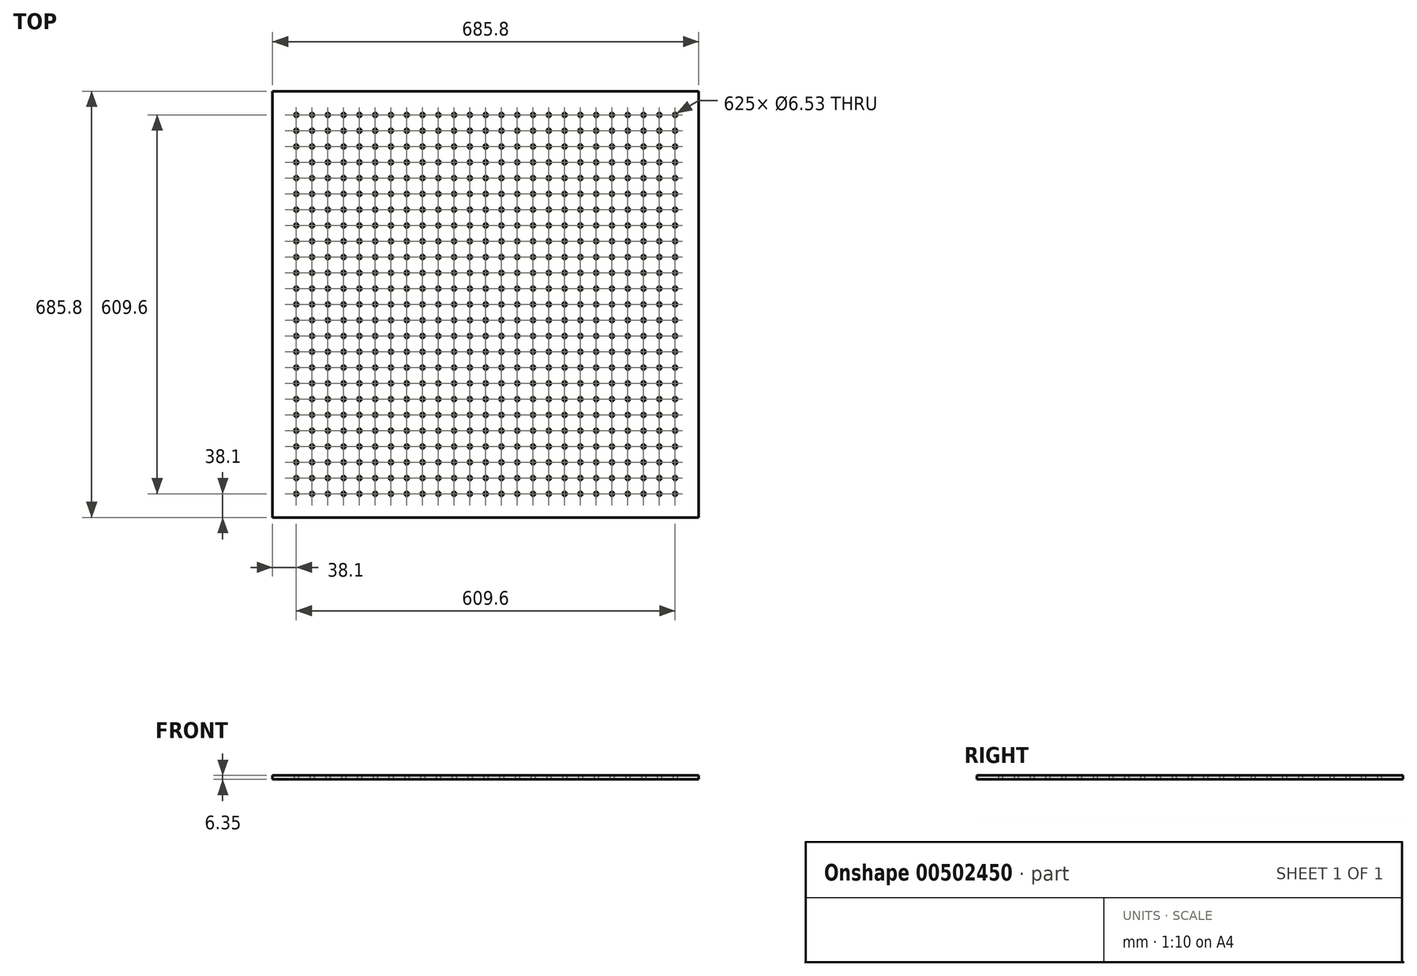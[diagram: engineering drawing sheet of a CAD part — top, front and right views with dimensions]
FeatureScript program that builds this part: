
annotation { "Feature Type Name" : "Feature", "Feature Type Description" : "" }
export const myFeature = defineFeature(function(context is Context, id is Id, definition is map)
    precondition{}
    {
        {
            var Q0;
            Q0=qCreatedBy(makeId("Top.planeOp"),FACE);
            var sketch = newSketch(context, id + "F0", { "sketchPlane" : qUnion([Q0])});
            skLineSegment(sketch, "E0.bottom", {"start": v(0, 685.8) * mm, "end": v(685.8, 685.8) * mm});
            skLineSegment(sketch, "E0.top", {"start": v(0, 0) * mm, "end": v(685.8, 0) * mm});
            skLineSegment(sketch, "E0.left", {"start": v(0, 685.8) * mm, "end": v(0, 0) * mm});
            skLineSegment(sketch, "E0.right", {"start": v(685.8, 685.8) * mm, "end": v(685.8, 0) * mm});
            skPoint(sketch, "E1", {"position": v(38.1, 38.1) * mm});
            skPoint(sketch, "E2.0.1.0", {"position": v(38.1, 63.5) * mm});
            skPoint(sketch, "E2.0.2.0", {"position": v(38.1, 88.9) * mm});
            skPoint(sketch, "E2.0.3.0", {"position": v(38.1, 114.3) * mm});
            skPoint(sketch, "E2.0.4.0", {"position": v(38.1, 139.7) * mm});
            skPoint(sketch, "E2.0.5.0", {"position": v(38.1, 165.1) * mm});
            skPoint(sketch, "E2.0.6.0", {"position": v(38.1, 190.5) * mm});
            skPoint(sketch, "E2.0.7.0", {"position": v(38.1, 215.9) * mm});
            skPoint(sketch, "E2.0.8.0", {"position": v(38.1, 241.3) * mm});
            skPoint(sketch, "E2.0.9.0", {"position": v(38.1, 266.7) * mm});
            skPoint(sketch, "E2.0.10.0", {"position": v(38.1, 292.1) * mm});
            skPoint(sketch, "E2.0.11.0", {"position": v(38.1, 317.5) * mm});
            skPoint(sketch, "E2.0.12.0", {"position": v(38.1, 342.9) * mm});
            skPoint(sketch, "E2.0.13.0", {"position": v(38.1, 368.3) * mm});
            skPoint(sketch, "E2.0.14.0", {"position": v(38.1, 393.7) * mm});
            skPoint(sketch, "E2.0.15.0", {"position": v(38.1, 419.1) * mm});
            skPoint(sketch, "E2.0.16.0", {"position": v(38.1, 444.5) * mm});
            skPoint(sketch, "E2.0.17.0", {"position": v(38.1, 469.9) * mm});
            skPoint(sketch, "E2.0.18.0", {"position": v(38.1, 495.3) * mm});
            skPoint(sketch, "E2.0.19.0", {"position": v(38.1, 520.7) * mm});
            skPoint(sketch, "E2.0.20.0", {"position": v(38.1, 546.1) * mm});
            skPoint(sketch, "E2.0.21.0", {"position": v(38.1, 571.5) * mm});
            skPoint(sketch, "E2.0.22.0", {"position": v(38.1, 596.9) * mm});
            skPoint(sketch, "E2.0.23.0", {"position": v(38.1, 622.3) * mm});
            skPoint(sketch, "E2.0.24.0", {"position": v(38.1, 647.7) * mm});
            skPoint(sketch, "E2.1.0.0", {"position": v(63.5, 38.1) * mm});
            skPoint(sketch, "E2.1.1.0", {"position": v(63.5, 63.5) * mm});
            skPoint(sketch, "E2.1.2.0", {"position": v(63.5, 88.9) * mm});
            skPoint(sketch, "E2.1.3.0", {"position": v(63.5, 114.3) * mm});
            skPoint(sketch, "E2.1.4.0", {"position": v(63.5, 139.7) * mm});
            skPoint(sketch, "E2.1.5.0", {"position": v(63.5, 165.1) * mm});
            skPoint(sketch, "E2.1.6.0", {"position": v(63.5, 190.5) * mm});
            skPoint(sketch, "E2.1.7.0", {"position": v(63.5, 215.9) * mm});
            skPoint(sketch, "E2.1.8.0", {"position": v(63.5, 241.3) * mm});
            skPoint(sketch, "E2.1.9.0", {"position": v(63.5, 266.7) * mm});
            skPoint(sketch, "E2.1.10.0", {"position": v(63.5, 292.1) * mm});
            skPoint(sketch, "E2.1.11.0", {"position": v(63.5, 317.5) * mm});
            skPoint(sketch, "E2.1.12.0", {"position": v(63.5, 342.9) * mm});
            skPoint(sketch, "E2.1.13.0", {"position": v(63.5, 368.3) * mm});
            skPoint(sketch, "E2.1.14.0", {"position": v(63.5, 393.7) * mm});
            skPoint(sketch, "E2.1.15.0", {"position": v(63.5, 419.1) * mm});
            skPoint(sketch, "E2.1.16.0", {"position": v(63.5, 444.5) * mm});
            skPoint(sketch, "E2.1.17.0", {"position": v(63.5, 469.9) * mm});
            skPoint(sketch, "E2.1.18.0", {"position": v(63.5, 495.3) * mm});
            skPoint(sketch, "E2.1.19.0", {"position": v(63.5, 520.7) * mm});
            skPoint(sketch, "E2.1.20.0", {"position": v(63.5, 546.1) * mm});
            skPoint(sketch, "E2.1.21.0", {"position": v(63.5, 571.5) * mm});
            skPoint(sketch, "E2.1.22.0", {"position": v(63.5, 596.9) * mm});
            skPoint(sketch, "E2.1.23.0", {"position": v(63.5, 622.3) * mm});
            skPoint(sketch, "E2.1.24.0", {"position": v(63.5, 647.7) * mm});
            skPoint(sketch, "E2.2.0.0", {"position": v(88.9, 38.1) * mm});
            skPoint(sketch, "E2.2.1.0", {"position": v(88.9, 63.5) * mm});
            skPoint(sketch, "E2.2.2.0", {"position": v(88.9, 88.9) * mm});
            skPoint(sketch, "E2.2.3.0", {"position": v(88.9, 114.3) * mm});
            skPoint(sketch, "E2.2.4.0", {"position": v(88.9, 139.7) * mm});
            skPoint(sketch, "E2.2.5.0", {"position": v(88.9, 165.1) * mm});
            skPoint(sketch, "E2.2.6.0", {"position": v(88.9, 190.5) * mm});
            skPoint(sketch, "E2.2.7.0", {"position": v(88.9, 215.9) * mm});
            skPoint(sketch, "E2.2.8.0", {"position": v(88.9, 241.3) * mm});
            skPoint(sketch, "E2.2.9.0", {"position": v(88.9, 266.7) * mm});
            skPoint(sketch, "E2.2.10.0", {"position": v(88.9, 292.1) * mm});
            skPoint(sketch, "E2.2.11.0", {"position": v(88.9, 317.5) * mm});
            skPoint(sketch, "E2.2.12.0", {"position": v(88.9, 342.9) * mm});
            skPoint(sketch, "E2.2.13.0", {"position": v(88.9, 368.3) * mm});
            skPoint(sketch, "E2.2.14.0", {"position": v(88.9, 393.7) * mm});
            skPoint(sketch, "E2.2.15.0", {"position": v(88.9, 419.1) * mm});
            skPoint(sketch, "E2.2.16.0", {"position": v(88.9, 444.5) * mm});
            skPoint(sketch, "E2.2.17.0", {"position": v(88.9, 469.9) * mm});
            skPoint(sketch, "E2.2.18.0", {"position": v(88.9, 495.3) * mm});
            skPoint(sketch, "E2.2.19.0", {"position": v(88.9, 520.7) * mm});
            skPoint(sketch, "E2.2.20.0", {"position": v(88.9, 546.1) * mm});
            skPoint(sketch, "E2.2.21.0", {"position": v(88.9, 571.5) * mm});
            skPoint(sketch, "E2.2.22.0", {"position": v(88.9, 596.9) * mm});
            skPoint(sketch, "E2.2.23.0", {"position": v(88.9, 622.3) * mm});
            skPoint(sketch, "E2.2.24.0", {"position": v(88.9, 647.7) * mm});
            skPoint(sketch, "E2.3.0.0", {"position": v(114.3, 38.1) * mm});
            skPoint(sketch, "E2.3.1.0", {"position": v(114.3, 63.5) * mm});
            skPoint(sketch, "E2.3.2.0", {"position": v(114.3, 88.9) * mm});
            skPoint(sketch, "E2.3.3.0", {"position": v(114.3, 114.3) * mm});
            skPoint(sketch, "E2.3.4.0", {"position": v(114.3, 139.7) * mm});
            skPoint(sketch, "E2.3.5.0", {"position": v(114.3, 165.1) * mm});
            skPoint(sketch, "E2.3.6.0", {"position": v(114.3, 190.5) * mm});
            skPoint(sketch, "E2.3.7.0", {"position": v(114.3, 215.9) * mm});
            skPoint(sketch, "E2.3.8.0", {"position": v(114.3, 241.3) * mm});
            skPoint(sketch, "E2.3.9.0", {"position": v(114.3, 266.7) * mm});
            skPoint(sketch, "E2.3.10.0", {"position": v(114.3, 292.1) * mm});
            skPoint(sketch, "E2.3.11.0", {"position": v(114.3, 317.5) * mm});
            skPoint(sketch, "E2.3.12.0", {"position": v(114.3, 342.9) * mm});
            skPoint(sketch, "E2.3.13.0", {"position": v(114.3, 368.3) * mm});
            skPoint(sketch, "E2.3.14.0", {"position": v(114.3, 393.7) * mm});
            skPoint(sketch, "E2.3.15.0", {"position": v(114.3, 419.1) * mm});
            skPoint(sketch, "E2.3.16.0", {"position": v(114.3, 444.5) * mm});
            skPoint(sketch, "E2.3.17.0", {"position": v(114.3, 469.9) * mm});
            skPoint(sketch, "E2.3.18.0", {"position": v(114.3, 495.3) * mm});
            skPoint(sketch, "E2.3.19.0", {"position": v(114.3, 520.7) * mm});
            skPoint(sketch, "E2.3.20.0", {"position": v(114.3, 546.1) * mm});
            skPoint(sketch, "E2.3.21.0", {"position": v(114.3, 571.5) * mm});
            skPoint(sketch, "E2.3.22.0", {"position": v(114.3, 596.9) * mm});
            skPoint(sketch, "E2.3.23.0", {"position": v(114.3, 622.3) * mm});
            skPoint(sketch, "E2.3.24.0", {"position": v(114.3, 647.7) * mm});
            skPoint(sketch, "E2.4.0.0", {"position": v(139.7, 38.1) * mm});
            skPoint(sketch, "E2.4.1.0", {"position": v(139.7, 63.5) * mm});
            skPoint(sketch, "E2.4.2.0", {"position": v(139.7, 88.9) * mm});
            skPoint(sketch, "E2.4.3.0", {"position": v(139.7, 114.3) * mm});
            skPoint(sketch, "E2.4.4.0", {"position": v(139.7, 139.7) * mm});
            skPoint(sketch, "E2.4.5.0", {"position": v(139.7, 165.1) * mm});
            skPoint(sketch, "E2.4.6.0", {"position": v(139.7, 190.5) * mm});
            skPoint(sketch, "E2.4.7.0", {"position": v(139.7, 215.9) * mm});
            skPoint(sketch, "E2.4.8.0", {"position": v(139.7, 241.3) * mm});
            skPoint(sketch, "E2.4.9.0", {"position": v(139.7, 266.7) * mm});
            skPoint(sketch, "E2.4.10.0", {"position": v(139.7, 292.1) * mm});
            skPoint(sketch, "E2.4.11.0", {"position": v(139.7, 317.5) * mm});
            skPoint(sketch, "E2.4.12.0", {"position": v(139.7, 342.9) * mm});
            skPoint(sketch, "E2.4.13.0", {"position": v(139.7, 368.3) * mm});
            skPoint(sketch, "E2.4.14.0", {"position": v(139.7, 393.7) * mm});
            skPoint(sketch, "E2.4.15.0", {"position": v(139.7, 419.1) * mm});
            skPoint(sketch, "E2.4.16.0", {"position": v(139.7, 444.5) * mm});
            skPoint(sketch, "E2.4.17.0", {"position": v(139.7, 469.9) * mm});
            skPoint(sketch, "E2.4.18.0", {"position": v(139.7, 495.3) * mm});
            skPoint(sketch, "E2.4.19.0", {"position": v(139.7, 520.7) * mm});
            skPoint(sketch, "E2.4.20.0", {"position": v(139.7, 546.1) * mm});
            skPoint(sketch, "E2.4.21.0", {"position": v(139.7, 571.5) * mm});
            skPoint(sketch, "E2.4.22.0", {"position": v(139.7, 596.9) * mm});
            skPoint(sketch, "E2.4.23.0", {"position": v(139.7, 622.3) * mm});
            skPoint(sketch, "E2.4.24.0", {"position": v(139.7, 647.7) * mm});
            skPoint(sketch, "E2.5.0.0", {"position": v(165.1, 38.1) * mm});
            skPoint(sketch, "E2.5.1.0", {"position": v(165.1, 63.5) * mm});
            skPoint(sketch, "E2.5.2.0", {"position": v(165.1, 88.9) * mm});
            skPoint(sketch, "E2.5.3.0", {"position": v(165.1, 114.3) * mm});
            skPoint(sketch, "E2.5.4.0", {"position": v(165.1, 139.7) * mm});
            skPoint(sketch, "E2.5.5.0", {"position": v(165.1, 165.1) * mm});
            skPoint(sketch, "E2.5.6.0", {"position": v(165.1, 190.5) * mm});
            skPoint(sketch, "E2.5.7.0", {"position": v(165.1, 215.9) * mm});
            skPoint(sketch, "E2.5.8.0", {"position": v(165.1, 241.3) * mm});
            skPoint(sketch, "E2.5.9.0", {"position": v(165.1, 266.7) * mm});
            skPoint(sketch, "E2.5.10.0", {"position": v(165.1, 292.1) * mm});
            skPoint(sketch, "E2.5.11.0", {"position": v(165.1, 317.5) * mm});
            skPoint(sketch, "E2.5.12.0", {"position": v(165.1, 342.9) * mm});
            skPoint(sketch, "E2.5.13.0", {"position": v(165.1, 368.3) * mm});
            skPoint(sketch, "E2.5.14.0", {"position": v(165.1, 393.7) * mm});
            skPoint(sketch, "E2.5.15.0", {"position": v(165.1, 419.1) * mm});
            skPoint(sketch, "E2.5.16.0", {"position": v(165.1, 444.5) * mm});
            skPoint(sketch, "E2.5.17.0", {"position": v(165.1, 469.9) * mm});
            skPoint(sketch, "E2.5.18.0", {"position": v(165.1, 495.3) * mm});
            skPoint(sketch, "E2.5.19.0", {"position": v(165.1, 520.7) * mm});
            skPoint(sketch, "E2.5.20.0", {"position": v(165.1, 546.1) * mm});
            skPoint(sketch, "E2.5.21.0", {"position": v(165.1, 571.5) * mm});
            skPoint(sketch, "E2.5.22.0", {"position": v(165.1, 596.9) * mm});
            skPoint(sketch, "E2.5.23.0", {"position": v(165.1, 622.3) * mm});
            skPoint(sketch, "E2.5.24.0", {"position": v(165.1, 647.7) * mm});
            skPoint(sketch, "E2.6.0.0", {"position": v(190.5, 38.1) * mm});
            skPoint(sketch, "E2.6.1.0", {"position": v(190.5, 63.5) * mm});
            skPoint(sketch, "E2.6.2.0", {"position": v(190.5, 88.9) * mm});
            skPoint(sketch, "E2.6.3.0", {"position": v(190.5, 114.3) * mm});
            skPoint(sketch, "E2.6.4.0", {"position": v(190.5, 139.7) * mm});
            skPoint(sketch, "E2.6.5.0", {"position": v(190.5, 165.1) * mm});
            skPoint(sketch, "E2.6.6.0", {"position": v(190.5, 190.5) * mm});
            skPoint(sketch, "E2.6.7.0", {"position": v(190.5, 215.9) * mm});
            skPoint(sketch, "E2.6.8.0", {"position": v(190.5, 241.3) * mm});
            skPoint(sketch, "E2.6.9.0", {"position": v(190.5, 266.7) * mm});
            skPoint(sketch, "E2.6.10.0", {"position": v(190.5, 292.1) * mm});
            skPoint(sketch, "E2.6.11.0", {"position": v(190.5, 317.5) * mm});
            skPoint(sketch, "E2.6.12.0", {"position": v(190.5, 342.9) * mm});
            skPoint(sketch, "E2.6.13.0", {"position": v(190.5, 368.3) * mm});
            skPoint(sketch, "E2.6.14.0", {"position": v(190.5, 393.7) * mm});
            skPoint(sketch, "E2.6.15.0", {"position": v(190.5, 419.1) * mm});
            skPoint(sketch, "E2.6.16.0", {"position": v(190.5, 444.5) * mm});
            skPoint(sketch, "E2.6.17.0", {"position": v(190.5, 469.9) * mm});
            skPoint(sketch, "E2.6.18.0", {"position": v(190.5, 495.3) * mm});
            skPoint(sketch, "E2.6.19.0", {"position": v(190.5, 520.7) * mm});
            skPoint(sketch, "E2.6.20.0", {"position": v(190.5, 546.1) * mm});
            skPoint(sketch, "E2.6.21.0", {"position": v(190.5, 571.5) * mm});
            skPoint(sketch, "E2.6.22.0", {"position": v(190.5, 596.9) * mm});
            skPoint(sketch, "E2.6.23.0", {"position": v(190.5, 622.3) * mm});
            skPoint(sketch, "E2.6.24.0", {"position": v(190.5, 647.7) * mm});
            skPoint(sketch, "E2.7.0.0", {"position": v(215.9, 38.1) * mm});
            skPoint(sketch, "E2.7.1.0", {"position": v(215.9, 63.5) * mm});
            skPoint(sketch, "E2.7.2.0", {"position": v(215.9, 88.9) * mm});
            skPoint(sketch, "E2.7.3.0", {"position": v(215.9, 114.3) * mm});
            skPoint(sketch, "E2.7.4.0", {"position": v(215.9, 139.7) * mm});
            skPoint(sketch, "E2.7.5.0", {"position": v(215.9, 165.1) * mm});
            skPoint(sketch, "E2.7.6.0", {"position": v(215.9, 190.5) * mm});
            skPoint(sketch, "E2.7.7.0", {"position": v(215.9, 215.9) * mm});
            skPoint(sketch, "E2.7.8.0", {"position": v(215.9, 241.3) * mm});
            skPoint(sketch, "E2.7.9.0", {"position": v(215.9, 266.7) * mm});
            skPoint(sketch, "E2.7.10.0", {"position": v(215.9, 292.1) * mm});
            skPoint(sketch, "E2.7.11.0", {"position": v(215.9, 317.5) * mm});
            skPoint(sketch, "E2.7.12.0", {"position": v(215.9, 342.9) * mm});
            skPoint(sketch, "E2.7.13.0", {"position": v(215.9, 368.3) * mm});
            skPoint(sketch, "E2.7.14.0", {"position": v(215.9, 393.7) * mm});
            skPoint(sketch, "E2.7.15.0", {"position": v(215.9, 419.1) * mm});
            skPoint(sketch, "E2.7.16.0", {"position": v(215.9, 444.5) * mm});
            skPoint(sketch, "E2.7.17.0", {"position": v(215.9, 469.9) * mm});
            skPoint(sketch, "E2.7.18.0", {"position": v(215.9, 495.3) * mm});
            skPoint(sketch, "E2.7.19.0", {"position": v(215.9, 520.7) * mm});
            skPoint(sketch, "E2.7.20.0", {"position": v(215.9, 546.1) * mm});
            skPoint(sketch, "E2.7.21.0", {"position": v(215.9, 571.5) * mm});
            skPoint(sketch, "E2.7.22.0", {"position": v(215.9, 596.9) * mm});
            skPoint(sketch, "E2.7.23.0", {"position": v(215.9, 622.3) * mm});
            skPoint(sketch, "E2.7.24.0", {"position": v(215.9, 647.7) * mm});
            skPoint(sketch, "E2.8.0.0", {"position": v(241.3, 38.1) * mm});
            skPoint(sketch, "E2.8.1.0", {"position": v(241.3, 63.5) * mm});
            skPoint(sketch, "E2.8.2.0", {"position": v(241.3, 88.9) * mm});
            skPoint(sketch, "E2.8.3.0", {"position": v(241.3, 114.3) * mm});
            skPoint(sketch, "E2.8.4.0", {"position": v(241.3, 139.7) * mm});
            skPoint(sketch, "E2.8.5.0", {"position": v(241.3, 165.1) * mm});
            skPoint(sketch, "E2.8.6.0", {"position": v(241.3, 190.5) * mm});
            skPoint(sketch, "E2.8.7.0", {"position": v(241.3, 215.9) * mm});
            skPoint(sketch, "E2.8.8.0", {"position": v(241.3, 241.3) * mm});
            skPoint(sketch, "E2.8.9.0", {"position": v(241.3, 266.7) * mm});
            skPoint(sketch, "E2.8.10.0", {"position": v(241.3, 292.1) * mm});
            skPoint(sketch, "E2.8.11.0", {"position": v(241.3, 317.5) * mm});
            skPoint(sketch, "E2.8.12.0", {"position": v(241.3, 342.9) * mm});
            skPoint(sketch, "E2.8.13.0", {"position": v(241.3, 368.3) * mm});
            skPoint(sketch, "E2.8.14.0", {"position": v(241.3, 393.7) * mm});
            skPoint(sketch, "E2.8.15.0", {"position": v(241.3, 419.1) * mm});
            skPoint(sketch, "E2.8.16.0", {"position": v(241.3, 444.5) * mm});
            skPoint(sketch, "E2.8.17.0", {"position": v(241.3, 469.9) * mm});
            skPoint(sketch, "E2.8.18.0", {"position": v(241.3, 495.3) * mm});
            skPoint(sketch, "E2.8.19.0", {"position": v(241.3, 520.7) * mm});
            skPoint(sketch, "E2.8.20.0", {"position": v(241.3, 546.1) * mm});
            skPoint(sketch, "E2.8.21.0", {"position": v(241.3, 571.5) * mm});
            skPoint(sketch, "E2.8.22.0", {"position": v(241.3, 596.9) * mm});
            skPoint(sketch, "E2.8.23.0", {"position": v(241.3, 622.3) * mm});
            skPoint(sketch, "E2.8.24.0", {"position": v(241.3, 647.7) * mm});
            skPoint(sketch, "E2.9.0.0", {"position": v(266.7, 38.1) * mm});
            skPoint(sketch, "E2.9.1.0", {"position": v(266.7, 63.5) * mm});
            skPoint(sketch, "E2.9.2.0", {"position": v(266.7, 88.9) * mm});
            skPoint(sketch, "E2.9.3.0", {"position": v(266.7, 114.3) * mm});
            skPoint(sketch, "E2.9.4.0", {"position": v(266.7, 139.7) * mm});
            skPoint(sketch, "E2.9.5.0", {"position": v(266.7, 165.1) * mm});
            skPoint(sketch, "E2.9.6.0", {"position": v(266.7, 190.5) * mm});
            skPoint(sketch, "E2.9.7.0", {"position": v(266.7, 215.9) * mm});
            skPoint(sketch, "E2.9.8.0", {"position": v(266.7, 241.3) * mm});
            skPoint(sketch, "E2.9.9.0", {"position": v(266.7, 266.7) * mm});
            skPoint(sketch, "E2.9.10.0", {"position": v(266.7, 292.1) * mm});
            skPoint(sketch, "E2.9.11.0", {"position": v(266.7, 317.5) * mm});
            skPoint(sketch, "E2.9.12.0", {"position": v(266.7, 342.9) * mm});
            skPoint(sketch, "E2.9.13.0", {"position": v(266.7, 368.3) * mm});
            skPoint(sketch, "E2.9.14.0", {"position": v(266.7, 393.7) * mm});
            skPoint(sketch, "E2.9.15.0", {"position": v(266.7, 419.1) * mm});
            skPoint(sketch, "E2.9.16.0", {"position": v(266.7, 444.5) * mm});
            skPoint(sketch, "E2.9.17.0", {"position": v(266.7, 469.9) * mm});
            skPoint(sketch, "E2.9.18.0", {"position": v(266.7, 495.3) * mm});
            skPoint(sketch, "E2.9.19.0", {"position": v(266.7, 520.7) * mm});
            skPoint(sketch, "E2.9.20.0", {"position": v(266.7, 546.1) * mm});
            skPoint(sketch, "E2.9.21.0", {"position": v(266.7, 571.5) * mm});
            skPoint(sketch, "E2.9.22.0", {"position": v(266.7, 596.9) * mm});
            skPoint(sketch, "E2.9.23.0", {"position": v(266.7, 622.3) * mm});
            skPoint(sketch, "E2.9.24.0", {"position": v(266.7, 647.7) * mm});
            skPoint(sketch, "E2.10.0.0", {"position": v(292.1, 38.1) * mm});
            skPoint(sketch, "E2.10.1.0", {"position": v(292.1, 63.5) * mm});
            skPoint(sketch, "E2.10.2.0", {"position": v(292.1, 88.9) * mm});
            skPoint(sketch, "E2.10.3.0", {"position": v(292.1, 114.3) * mm});
            skPoint(sketch, "E2.10.4.0", {"position": v(292.1, 139.7) * mm});
            skPoint(sketch, "E2.10.5.0", {"position": v(292.1, 165.1) * mm});
            skPoint(sketch, "E2.10.6.0", {"position": v(292.1, 190.5) * mm});
            skPoint(sketch, "E2.10.7.0", {"position": v(292.1, 215.9) * mm});
            skPoint(sketch, "E2.10.8.0", {"position": v(292.1, 241.3) * mm});
            skPoint(sketch, "E2.10.9.0", {"position": v(292.1, 266.7) * mm});
            skPoint(sketch, "E2.10.10.0", {"position": v(292.1, 292.1) * mm});
            skPoint(sketch, "E2.10.11.0", {"position": v(292.1, 317.5) * mm});
            skPoint(sketch, "E2.10.12.0", {"position": v(292.1, 342.9) * mm});
            skPoint(sketch, "E2.10.13.0", {"position": v(292.1, 368.3) * mm});
            skPoint(sketch, "E2.10.14.0", {"position": v(292.1, 393.7) * mm});
            skPoint(sketch, "E2.10.15.0", {"position": v(292.1, 419.1) * mm});
            skPoint(sketch, "E2.10.16.0", {"position": v(292.1, 444.5) * mm});
            skPoint(sketch, "E2.10.17.0", {"position": v(292.1, 469.9) * mm});
            skPoint(sketch, "E2.10.18.0", {"position": v(292.1, 495.3) * mm});
            skPoint(sketch, "E2.10.19.0", {"position": v(292.1, 520.7) * mm});
            skPoint(sketch, "E2.10.20.0", {"position": v(292.1, 546.1) * mm});
            skPoint(sketch, "E2.10.21.0", {"position": v(292.1, 571.5) * mm});
            skPoint(sketch, "E2.10.22.0", {"position": v(292.1, 596.9) * mm});
            skPoint(sketch, "E2.10.23.0", {"position": v(292.1, 622.3) * mm});
            skPoint(sketch, "E2.10.24.0", {"position": v(292.1, 647.7) * mm});
            skPoint(sketch, "E2.11.0.0", {"position": v(317.5, 38.1) * mm});
            skPoint(sketch, "E2.11.1.0", {"position": v(317.5, 63.5) * mm});
            skPoint(sketch, "E2.11.2.0", {"position": v(317.5, 88.9) * mm});
            skPoint(sketch, "E2.11.3.0", {"position": v(317.5, 114.3) * mm});
            skPoint(sketch, "E2.11.4.0", {"position": v(317.5, 139.7) * mm});
            skPoint(sketch, "E2.11.5.0", {"position": v(317.5, 165.1) * mm});
            skPoint(sketch, "E2.11.6.0", {"position": v(317.5, 190.5) * mm});
            skPoint(sketch, "E2.11.7.0", {"position": v(317.5, 215.9) * mm});
            skPoint(sketch, "E2.11.8.0", {"position": v(317.5, 241.3) * mm});
            skPoint(sketch, "E2.11.9.0", {"position": v(317.5, 266.7) * mm});
            skPoint(sketch, "E2.11.10.0", {"position": v(317.5, 292.1) * mm});
            skPoint(sketch, "E2.11.11.0", {"position": v(317.5, 317.5) * mm});
            skPoint(sketch, "E2.11.12.0", {"position": v(317.5, 342.9) * mm});
            skPoint(sketch, "E2.11.13.0", {"position": v(317.5, 368.3) * mm});
            skPoint(sketch, "E2.11.14.0", {"position": v(317.5, 393.7) * mm});
            skPoint(sketch, "E2.11.15.0", {"position": v(317.5, 419.1) * mm});
            skPoint(sketch, "E2.11.16.0", {"position": v(317.5, 444.5) * mm});
            skPoint(sketch, "E2.11.17.0", {"position": v(317.5, 469.9) * mm});
            skPoint(sketch, "E2.11.18.0", {"position": v(317.5, 495.3) * mm});
            skPoint(sketch, "E2.11.19.0", {"position": v(317.5, 520.7) * mm});
            skPoint(sketch, "E2.11.20.0", {"position": v(317.5, 546.1) * mm});
            skPoint(sketch, "E2.11.21.0", {"position": v(317.5, 571.5) * mm});
            skPoint(sketch, "E2.11.22.0", {"position": v(317.5, 596.9) * mm});
            skPoint(sketch, "E2.11.23.0", {"position": v(317.5, 622.3) * mm});
            skPoint(sketch, "E2.11.24.0", {"position": v(317.5, 647.7) * mm});
            skPoint(sketch, "E2.12.0.0", {"position": v(342.9, 38.1) * mm});
            skPoint(sketch, "E2.12.1.0", {"position": v(342.9, 63.5) * mm});
            skPoint(sketch, "E2.12.2.0", {"position": v(342.9, 88.9) * mm});
            skPoint(sketch, "E2.12.3.0", {"position": v(342.9, 114.3) * mm});
            skPoint(sketch, "E2.12.4.0", {"position": v(342.9, 139.7) * mm});
            skPoint(sketch, "E2.12.5.0", {"position": v(342.9, 165.1) * mm});
            skPoint(sketch, "E2.12.6.0", {"position": v(342.9, 190.5) * mm});
            skPoint(sketch, "E2.12.7.0", {"position": v(342.9, 215.9) * mm});
            skPoint(sketch, "E2.12.8.0", {"position": v(342.9, 241.3) * mm});
            skPoint(sketch, "E2.12.9.0", {"position": v(342.9, 266.7) * mm});
            skPoint(sketch, "E2.12.10.0", {"position": v(342.9, 292.1) * mm});
            skPoint(sketch, "E2.12.11.0", {"position": v(342.9, 317.5) * mm});
            skPoint(sketch, "E2.12.12.0", {"position": v(342.9, 342.9) * mm});
            skPoint(sketch, "E2.12.13.0", {"position": v(342.9, 368.3) * mm});
            skPoint(sketch, "E2.12.14.0", {"position": v(342.9, 393.7) * mm});
            skPoint(sketch, "E2.12.15.0", {"position": v(342.9, 419.1) * mm});
            skPoint(sketch, "E2.12.16.0", {"position": v(342.9, 444.5) * mm});
            skPoint(sketch, "E2.12.17.0", {"position": v(342.9, 469.9) * mm});
            skPoint(sketch, "E2.12.18.0", {"position": v(342.9, 495.3) * mm});
            skPoint(sketch, "E2.12.19.0", {"position": v(342.9, 520.7) * mm});
            skPoint(sketch, "E2.12.20.0", {"position": v(342.9, 546.1) * mm});
            skPoint(sketch, "E2.12.21.0", {"position": v(342.9, 571.5) * mm});
            skPoint(sketch, "E2.12.22.0", {"position": v(342.9, 596.9) * mm});
            skPoint(sketch, "E2.12.23.0", {"position": v(342.9, 622.3) * mm});
            skPoint(sketch, "E2.12.24.0", {"position": v(342.9, 647.7) * mm});
            skPoint(sketch, "E2.13.0.0", {"position": v(368.3, 38.1) * mm});
            skPoint(sketch, "E2.13.1.0", {"position": v(368.3, 63.5) * mm});
            skPoint(sketch, "E2.13.2.0", {"position": v(368.3, 88.9) * mm});
            skPoint(sketch, "E2.13.3.0", {"position": v(368.3, 114.3) * mm});
            skPoint(sketch, "E2.13.4.0", {"position": v(368.3, 139.7) * mm});
            skPoint(sketch, "E2.13.5.0", {"position": v(368.3, 165.1) * mm});
            skPoint(sketch, "E2.13.6.0", {"position": v(368.3, 190.5) * mm});
            skPoint(sketch, "E2.13.7.0", {"position": v(368.3, 215.9) * mm});
            skPoint(sketch, "E2.13.8.0", {"position": v(368.3, 241.3) * mm});
            skPoint(sketch, "E2.13.9.0", {"position": v(368.3, 266.7) * mm});
            skPoint(sketch, "E2.13.10.0", {"position": v(368.3, 292.1) * mm});
            skPoint(sketch, "E2.13.11.0", {"position": v(368.3, 317.5) * mm});
            skPoint(sketch, "E2.13.12.0", {"position": v(368.3, 342.9) * mm});
            skPoint(sketch, "E2.13.13.0", {"position": v(368.3, 368.3) * mm});
            skPoint(sketch, "E2.13.14.0", {"position": v(368.3, 393.7) * mm});
            skPoint(sketch, "E2.13.15.0", {"position": v(368.3, 419.1) * mm});
            skPoint(sketch, "E2.13.16.0", {"position": v(368.3, 444.5) * mm});
            skPoint(sketch, "E2.13.17.0", {"position": v(368.3, 469.9) * mm});
            skPoint(sketch, "E2.13.18.0", {"position": v(368.3, 495.3) * mm});
            skPoint(sketch, "E2.13.19.0", {"position": v(368.3, 520.7) * mm});
            skPoint(sketch, "E2.13.20.0", {"position": v(368.3, 546.1) * mm});
            skPoint(sketch, "E2.13.21.0", {"position": v(368.3, 571.5) * mm});
            skPoint(sketch, "E2.13.22.0", {"position": v(368.3, 596.9) * mm});
            skPoint(sketch, "E2.13.23.0", {"position": v(368.3, 622.3) * mm});
            skPoint(sketch, "E2.13.24.0", {"position": v(368.3, 647.7) * mm});
            skPoint(sketch, "E2.14.0.0", {"position": v(393.7, 38.1) * mm});
            skPoint(sketch, "E2.14.1.0", {"position": v(393.7, 63.5) * mm});
            skPoint(sketch, "E2.14.2.0", {"position": v(393.7, 88.9) * mm});
            skPoint(sketch, "E2.14.3.0", {"position": v(393.7, 114.3) * mm});
            skPoint(sketch, "E2.14.4.0", {"position": v(393.7, 139.7) * mm});
            skPoint(sketch, "E2.14.5.0", {"position": v(393.7, 165.1) * mm});
            skPoint(sketch, "E2.14.6.0", {"position": v(393.7, 190.5) * mm});
            skPoint(sketch, "E2.14.7.0", {"position": v(393.7, 215.9) * mm});
            skPoint(sketch, "E2.14.8.0", {"position": v(393.7, 241.3) * mm});
            skPoint(sketch, "E2.14.9.0", {"position": v(393.7, 266.7) * mm});
            skPoint(sketch, "E2.14.10.0", {"position": v(393.7, 292.1) * mm});
            skPoint(sketch, "E2.14.11.0", {"position": v(393.7, 317.5) * mm});
            skPoint(sketch, "E2.14.12.0", {"position": v(393.7, 342.9) * mm});
            skPoint(sketch, "E2.14.13.0", {"position": v(393.7, 368.3) * mm});
            skPoint(sketch, "E2.14.14.0", {"position": v(393.7, 393.7) * mm});
            skPoint(sketch, "E2.14.15.0", {"position": v(393.7, 419.1) * mm});
            skPoint(sketch, "E2.14.16.0", {"position": v(393.7, 444.5) * mm});
            skPoint(sketch, "E2.14.17.0", {"position": v(393.7, 469.9) * mm});
            skPoint(sketch, "E2.14.18.0", {"position": v(393.7, 495.3) * mm});
            skPoint(sketch, "E2.14.19.0", {"position": v(393.7, 520.7) * mm});
            skPoint(sketch, "E2.14.20.0", {"position": v(393.7, 546.1) * mm});
            skPoint(sketch, "E2.14.21.0", {"position": v(393.7, 571.5) * mm});
            skPoint(sketch, "E2.14.22.0", {"position": v(393.7, 596.9) * mm});
            skPoint(sketch, "E2.14.23.0", {"position": v(393.7, 622.3) * mm});
            skPoint(sketch, "E2.14.24.0", {"position": v(393.7, 647.7) * mm});
            skPoint(sketch, "E2.15.0.0", {"position": v(419.1, 38.1) * mm});
            skPoint(sketch, "E2.15.1.0", {"position": v(419.1, 63.5) * mm});
            skPoint(sketch, "E2.15.2.0", {"position": v(419.1, 88.9) * mm});
            skPoint(sketch, "E2.15.3.0", {"position": v(419.1, 114.3) * mm});
            skPoint(sketch, "E2.15.4.0", {"position": v(419.1, 139.7) * mm});
            skPoint(sketch, "E2.15.5.0", {"position": v(419.1, 165.1) * mm});
            skPoint(sketch, "E2.15.6.0", {"position": v(419.1, 190.5) * mm});
            skPoint(sketch, "E2.15.7.0", {"position": v(419.1, 215.9) * mm});
            skPoint(sketch, "E2.15.8.0", {"position": v(419.1, 241.3) * mm});
            skPoint(sketch, "E2.15.9.0", {"position": v(419.1, 266.7) * mm});
            skPoint(sketch, "E2.15.10.0", {"position": v(419.1, 292.1) * mm});
            skPoint(sketch, "E2.15.11.0", {"position": v(419.1, 317.5) * mm});
            skPoint(sketch, "E2.15.12.0", {"position": v(419.1, 342.9) * mm});
            skPoint(sketch, "E2.15.13.0", {"position": v(419.1, 368.3) * mm});
            skPoint(sketch, "E2.15.14.0", {"position": v(419.1, 393.7) * mm});
            skPoint(sketch, "E2.15.15.0", {"position": v(419.1, 419.1) * mm});
            skPoint(sketch, "E2.15.16.0", {"position": v(419.1, 444.5) * mm});
            skPoint(sketch, "E2.15.17.0", {"position": v(419.1, 469.9) * mm});
            skPoint(sketch, "E2.15.18.0", {"position": v(419.1, 495.3) * mm});
            skPoint(sketch, "E2.15.19.0", {"position": v(419.1, 520.7) * mm});
            skPoint(sketch, "E2.15.20.0", {"position": v(419.1, 546.1) * mm});
            skPoint(sketch, "E2.15.21.0", {"position": v(419.1, 571.5) * mm});
            skPoint(sketch, "E2.15.22.0", {"position": v(419.1, 596.9) * mm});
            skPoint(sketch, "E2.15.23.0", {"position": v(419.1, 622.3) * mm});
            skPoint(sketch, "E2.15.24.0", {"position": v(419.1, 647.7) * mm});
            skPoint(sketch, "E2.16.0.0", {"position": v(444.5, 38.1) * mm});
            skPoint(sketch, "E2.16.1.0", {"position": v(444.5, 63.5) * mm});
            skPoint(sketch, "E2.16.2.0", {"position": v(444.5, 88.9) * mm});
            skPoint(sketch, "E2.16.3.0", {"position": v(444.5, 114.3) * mm});
            skPoint(sketch, "E2.16.4.0", {"position": v(444.5, 139.7) * mm});
            skPoint(sketch, "E2.16.5.0", {"position": v(444.5, 165.1) * mm});
            skPoint(sketch, "E2.16.6.0", {"position": v(444.5, 190.5) * mm});
            skPoint(sketch, "E2.16.7.0", {"position": v(444.5, 215.9) * mm});
            skPoint(sketch, "E2.16.8.0", {"position": v(444.5, 241.3) * mm});
            skPoint(sketch, "E2.16.9.0", {"position": v(444.5, 266.7) * mm});
            skPoint(sketch, "E2.16.10.0", {"position": v(444.5, 292.1) * mm});
            skPoint(sketch, "E2.16.11.0", {"position": v(444.5, 317.5) * mm});
            skPoint(sketch, "E2.16.12.0", {"position": v(444.5, 342.9) * mm});
            skPoint(sketch, "E2.16.13.0", {"position": v(444.5, 368.3) * mm});
            skPoint(sketch, "E2.16.14.0", {"position": v(444.5, 393.7) * mm});
            skPoint(sketch, "E2.16.15.0", {"position": v(444.5, 419.1) * mm});
            skPoint(sketch, "E2.16.16.0", {"position": v(444.5, 444.5) * mm});
            skPoint(sketch, "E2.16.17.0", {"position": v(444.5, 469.9) * mm});
            skPoint(sketch, "E2.16.18.0", {"position": v(444.5, 495.3) * mm});
            skPoint(sketch, "E2.16.19.0", {"position": v(444.5, 520.7) * mm});
            skPoint(sketch, "E2.16.20.0", {"position": v(444.5, 546.1) * mm});
            skPoint(sketch, "E2.16.21.0", {"position": v(444.5, 571.5) * mm});
            skPoint(sketch, "E2.16.22.0", {"position": v(444.5, 596.9) * mm});
            skPoint(sketch, "E2.16.23.0", {"position": v(444.5, 622.3) * mm});
            skPoint(sketch, "E2.16.24.0", {"position": v(444.5, 647.7) * mm});
            skPoint(sketch, "E2.17.0.0", {"position": v(469.9, 38.1) * mm});
            skPoint(sketch, "E2.17.1.0", {"position": v(469.9, 63.5) * mm});
            skPoint(sketch, "E2.17.2.0", {"position": v(469.9, 88.9) * mm});
            skPoint(sketch, "E2.17.3.0", {"position": v(469.9, 114.3) * mm});
            skPoint(sketch, "E2.17.4.0", {"position": v(469.9, 139.7) * mm});
            skPoint(sketch, "E2.17.5.0", {"position": v(469.9, 165.1) * mm});
            skPoint(sketch, "E2.17.6.0", {"position": v(469.9, 190.5) * mm});
            skPoint(sketch, "E2.17.7.0", {"position": v(469.9, 215.9) * mm});
            skPoint(sketch, "E2.17.8.0", {"position": v(469.9, 241.3) * mm});
            skPoint(sketch, "E2.17.9.0", {"position": v(469.9, 266.7) * mm});
            skPoint(sketch, "E2.17.10.0", {"position": v(469.9, 292.1) * mm});
            skPoint(sketch, "E2.17.11.0", {"position": v(469.9, 317.5) * mm});
            skPoint(sketch, "E2.17.12.0", {"position": v(469.9, 342.9) * mm});
            skPoint(sketch, "E2.17.13.0", {"position": v(469.9, 368.3) * mm});
            skPoint(sketch, "E2.17.14.0", {"position": v(469.9, 393.7) * mm});
            skPoint(sketch, "E2.17.15.0", {"position": v(469.9, 419.1) * mm});
            skPoint(sketch, "E2.17.16.0", {"position": v(469.9, 444.5) * mm});
            skPoint(sketch, "E2.17.17.0", {"position": v(469.9, 469.9) * mm});
            skPoint(sketch, "E2.17.18.0", {"position": v(469.9, 495.3) * mm});
            skPoint(sketch, "E2.17.19.0", {"position": v(469.9, 520.7) * mm});
            skPoint(sketch, "E2.17.20.0", {"position": v(469.9, 546.1) * mm});
            skPoint(sketch, "E2.17.21.0", {"position": v(469.9, 571.5) * mm});
            skPoint(sketch, "E2.17.22.0", {"position": v(469.9, 596.9) * mm});
            skPoint(sketch, "E2.17.23.0", {"position": v(469.9, 622.3) * mm});
            skPoint(sketch, "E2.17.24.0", {"position": v(469.9, 647.7) * mm});
            skPoint(sketch, "E2.18.0.0", {"position": v(495.3, 38.1) * mm});
            skPoint(sketch, "E2.18.1.0", {"position": v(495.3, 63.5) * mm});
            skPoint(sketch, "E2.18.2.0", {"position": v(495.3, 88.9) * mm});
            skPoint(sketch, "E2.18.3.0", {"position": v(495.3, 114.3) * mm});
            skPoint(sketch, "E2.18.4.0", {"position": v(495.3, 139.7) * mm});
            skPoint(sketch, "E2.18.5.0", {"position": v(495.3, 165.1) * mm});
            skPoint(sketch, "E2.18.6.0", {"position": v(495.3, 190.5) * mm});
            skPoint(sketch, "E2.18.7.0", {"position": v(495.3, 215.9) * mm});
            skPoint(sketch, "E2.18.8.0", {"position": v(495.3, 241.3) * mm});
            skPoint(sketch, "E2.18.9.0", {"position": v(495.3, 266.7) * mm});
            skPoint(sketch, "E2.18.10.0", {"position": v(495.3, 292.1) * mm});
            skPoint(sketch, "E2.18.11.0", {"position": v(495.3, 317.5) * mm});
            skPoint(sketch, "E2.18.12.0", {"position": v(495.3, 342.9) * mm});
            skPoint(sketch, "E2.18.13.0", {"position": v(495.3, 368.3) * mm});
            skPoint(sketch, "E2.18.14.0", {"position": v(495.3, 393.7) * mm});
            skPoint(sketch, "E2.18.15.0", {"position": v(495.3, 419.1) * mm});
            skPoint(sketch, "E2.18.16.0", {"position": v(495.3, 444.5) * mm});
            skPoint(sketch, "E2.18.17.0", {"position": v(495.3, 469.9) * mm});
            skPoint(sketch, "E2.18.18.0", {"position": v(495.3, 495.3) * mm});
            skPoint(sketch, "E2.18.19.0", {"position": v(495.3, 520.7) * mm});
            skPoint(sketch, "E2.18.20.0", {"position": v(495.3, 546.1) * mm});
            skPoint(sketch, "E2.18.21.0", {"position": v(495.3, 571.5) * mm});
            skPoint(sketch, "E2.18.22.0", {"position": v(495.3, 596.9) * mm});
            skPoint(sketch, "E2.18.23.0", {"position": v(495.3, 622.3) * mm});
            skPoint(sketch, "E2.18.24.0", {"position": v(495.3, 647.7) * mm});
            skPoint(sketch, "E2.19.0.0", {"position": v(520.7, 38.1) * mm});
            skPoint(sketch, "E2.19.1.0", {"position": v(520.7, 63.5) * mm});
            skPoint(sketch, "E2.19.2.0", {"position": v(520.7, 88.9) * mm});
            skPoint(sketch, "E2.19.3.0", {"position": v(520.7, 114.3) * mm});
            skPoint(sketch, "E2.19.4.0", {"position": v(520.7, 139.7) * mm});
            skPoint(sketch, "E2.19.5.0", {"position": v(520.7, 165.1) * mm});
            skPoint(sketch, "E2.19.6.0", {"position": v(520.7, 190.5) * mm});
            skPoint(sketch, "E2.19.7.0", {"position": v(520.7, 215.9) * mm});
            skPoint(sketch, "E2.19.8.0", {"position": v(520.7, 241.3) * mm});
            skPoint(sketch, "E2.19.9.0", {"position": v(520.7, 266.7) * mm});
            skPoint(sketch, "E2.19.10.0", {"position": v(520.7, 292.1) * mm});
            skPoint(sketch, "E2.19.11.0", {"position": v(520.7, 317.5) * mm});
            skPoint(sketch, "E2.19.12.0", {"position": v(520.7, 342.9) * mm});
            skPoint(sketch, "E2.19.13.0", {"position": v(520.7, 368.3) * mm});
            skPoint(sketch, "E2.19.14.0", {"position": v(520.7, 393.7) * mm});
            skPoint(sketch, "E2.19.15.0", {"position": v(520.7, 419.1) * mm});
            skPoint(sketch, "E2.19.16.0", {"position": v(520.7, 444.5) * mm});
            skPoint(sketch, "E2.19.17.0", {"position": v(520.7, 469.9) * mm});
            skPoint(sketch, "E2.19.18.0", {"position": v(520.7, 495.3) * mm});
            skPoint(sketch, "E2.19.19.0", {"position": v(520.7, 520.7) * mm});
            skPoint(sketch, "E2.19.20.0", {"position": v(520.7, 546.1) * mm});
            skPoint(sketch, "E2.19.21.0", {"position": v(520.7, 571.5) * mm});
            skPoint(sketch, "E2.19.22.0", {"position": v(520.7, 596.9) * mm});
            skPoint(sketch, "E2.19.23.0", {"position": v(520.7, 622.3) * mm});
            skPoint(sketch, "E2.19.24.0", {"position": v(520.7, 647.7) * mm});
            skPoint(sketch, "E2.20.0.0", {"position": v(546.1, 38.1) * mm});
            skPoint(sketch, "E2.20.1.0", {"position": v(546.1, 63.5) * mm});
            skPoint(sketch, "E2.20.2.0", {"position": v(546.1, 88.9) * mm});
            skPoint(sketch, "E2.20.3.0", {"position": v(546.1, 114.3) * mm});
            skPoint(sketch, "E2.20.4.0", {"position": v(546.1, 139.7) * mm});
            skPoint(sketch, "E2.20.5.0", {"position": v(546.1, 165.1) * mm});
            skPoint(sketch, "E2.20.6.0", {"position": v(546.1, 190.5) * mm});
            skPoint(sketch, "E2.20.7.0", {"position": v(546.1, 215.9) * mm});
            skPoint(sketch, "E2.20.8.0", {"position": v(546.1, 241.3) * mm});
            skPoint(sketch, "E2.20.9.0", {"position": v(546.1, 266.7) * mm});
            skPoint(sketch, "E2.20.10.0", {"position": v(546.1, 292.1) * mm});
            skPoint(sketch, "E2.20.11.0", {"position": v(546.1, 317.5) * mm});
            skPoint(sketch, "E2.20.12.0", {"position": v(546.1, 342.9) * mm});
            skPoint(sketch, "E2.20.13.0", {"position": v(546.1, 368.3) * mm});
            skPoint(sketch, "E2.20.14.0", {"position": v(546.1, 393.7) * mm});
            skPoint(sketch, "E2.20.15.0", {"position": v(546.1, 419.1) * mm});
            skPoint(sketch, "E2.20.16.0", {"position": v(546.1, 444.5) * mm});
            skPoint(sketch, "E2.20.17.0", {"position": v(546.1, 469.9) * mm});
            skPoint(sketch, "E2.20.18.0", {"position": v(546.1, 495.3) * mm});
            skPoint(sketch, "E2.20.19.0", {"position": v(546.1, 520.7) * mm});
            skPoint(sketch, "E2.20.20.0", {"position": v(546.1, 546.1) * mm});
            skPoint(sketch, "E2.20.21.0", {"position": v(546.1, 571.5) * mm});
            skPoint(sketch, "E2.20.22.0", {"position": v(546.1, 596.9) * mm});
            skPoint(sketch, "E2.20.23.0", {"position": v(546.1, 622.3) * mm});
            skPoint(sketch, "E2.20.24.0", {"position": v(546.1, 647.7) * mm});
            skPoint(sketch, "E2.21.0.0", {"position": v(571.5, 38.1) * mm});
            skPoint(sketch, "E2.21.1.0", {"position": v(571.5, 63.5) * mm});
            skPoint(sketch, "E2.21.2.0", {"position": v(571.5, 88.9) * mm});
            skPoint(sketch, "E2.21.3.0", {"position": v(571.5, 114.3) * mm});
            skPoint(sketch, "E2.21.4.0", {"position": v(571.5, 139.7) * mm});
            skPoint(sketch, "E2.21.5.0", {"position": v(571.5, 165.1) * mm});
            skPoint(sketch, "E2.21.6.0", {"position": v(571.5, 190.5) * mm});
            skPoint(sketch, "E2.21.7.0", {"position": v(571.5, 215.9) * mm});
            skPoint(sketch, "E2.21.8.0", {"position": v(571.5, 241.3) * mm});
            skPoint(sketch, "E2.21.9.0", {"position": v(571.5, 266.7) * mm});
            skPoint(sketch, "E2.21.10.0", {"position": v(571.5, 292.1) * mm});
            skPoint(sketch, "E2.21.11.0", {"position": v(571.5, 317.5) * mm});
            skPoint(sketch, "E2.21.12.0", {"position": v(571.5, 342.9) * mm});
            skPoint(sketch, "E2.21.13.0", {"position": v(571.5, 368.3) * mm});
            skPoint(sketch, "E2.21.14.0", {"position": v(571.5, 393.7) * mm});
            skPoint(sketch, "E2.21.15.0", {"position": v(571.5, 419.1) * mm});
            skPoint(sketch, "E2.21.16.0", {"position": v(571.5, 444.5) * mm});
            skPoint(sketch, "E2.21.17.0", {"position": v(571.5, 469.9) * mm});
            skPoint(sketch, "E2.21.18.0", {"position": v(571.5, 495.3) * mm});
            skPoint(sketch, "E2.21.19.0", {"position": v(571.5, 520.7) * mm});
            skPoint(sketch, "E2.21.20.0", {"position": v(571.5, 546.1) * mm});
            skPoint(sketch, "E2.21.21.0", {"position": v(571.5, 571.5) * mm});
            skPoint(sketch, "E2.21.22.0", {"position": v(571.5, 596.9) * mm});
            skPoint(sketch, "E2.21.23.0", {"position": v(571.5, 622.3) * mm});
            skPoint(sketch, "E2.21.24.0", {"position": v(571.5, 647.7) * mm});
            skPoint(sketch, "E2.22.0.0", {"position": v(596.9, 38.1) * mm});
            skPoint(sketch, "E2.22.1.0", {"position": v(596.9, 63.5) * mm});
            skPoint(sketch, "E2.22.2.0", {"position": v(596.9, 88.9) * mm});
            skPoint(sketch, "E2.22.3.0", {"position": v(596.9, 114.3) * mm});
            skPoint(sketch, "E2.22.4.0", {"position": v(596.9, 139.7) * mm});
            skPoint(sketch, "E2.22.5.0", {"position": v(596.9, 165.1) * mm});
            skPoint(sketch, "E2.22.6.0", {"position": v(596.9, 190.5) * mm});
            skPoint(sketch, "E2.22.7.0", {"position": v(596.9, 215.9) * mm});
            skPoint(sketch, "E2.22.8.0", {"position": v(596.9, 241.3) * mm});
            skPoint(sketch, "E2.22.9.0", {"position": v(596.9, 266.7) * mm});
            skPoint(sketch, "E2.22.10.0", {"position": v(596.9, 292.1) * mm});
            skPoint(sketch, "E2.22.11.0", {"position": v(596.9, 317.5) * mm});
            skPoint(sketch, "E2.22.12.0", {"position": v(596.9, 342.9) * mm});
            skPoint(sketch, "E2.22.13.0", {"position": v(596.9, 368.3) * mm});
            skPoint(sketch, "E2.22.14.0", {"position": v(596.9, 393.7) * mm});
            skPoint(sketch, "E2.22.15.0", {"position": v(596.9, 419.1) * mm});
            skPoint(sketch, "E2.22.16.0", {"position": v(596.9, 444.5) * mm});
            skPoint(sketch, "E2.22.17.0", {"position": v(596.9, 469.9) * mm});
            skPoint(sketch, "E2.22.18.0", {"position": v(596.9, 495.3) * mm});
            skPoint(sketch, "E2.22.19.0", {"position": v(596.9, 520.7) * mm});
            skPoint(sketch, "E2.22.20.0", {"position": v(596.9, 546.1) * mm});
            skPoint(sketch, "E2.22.21.0", {"position": v(596.9, 571.5) * mm});
            skPoint(sketch, "E2.22.22.0", {"position": v(596.9, 596.9) * mm});
            skPoint(sketch, "E2.22.23.0", {"position": v(596.9, 622.3) * mm});
            skPoint(sketch, "E2.22.24.0", {"position": v(596.9, 647.7) * mm});
            skPoint(sketch, "E2.23.0.0", {"position": v(622.3, 38.1) * mm});
            skPoint(sketch, "E2.23.1.0", {"position": v(622.3, 63.5) * mm});
            skPoint(sketch, "E2.23.2.0", {"position": v(622.3, 88.9) * mm});
            skPoint(sketch, "E2.23.3.0", {"position": v(622.3, 114.3) * mm});
            skPoint(sketch, "E2.23.4.0", {"position": v(622.3, 139.7) * mm});
            skPoint(sketch, "E2.23.5.0", {"position": v(622.3, 165.1) * mm});
            skPoint(sketch, "E2.23.6.0", {"position": v(622.3, 190.5) * mm});
            skPoint(sketch, "E2.23.7.0", {"position": v(622.3, 215.9) * mm});
            skPoint(sketch, "E2.23.8.0", {"position": v(622.3, 241.3) * mm});
            skPoint(sketch, "E2.23.9.0", {"position": v(622.3, 266.7) * mm});
            skPoint(sketch, "E2.23.10.0", {"position": v(622.3, 292.1) * mm});
            skPoint(sketch, "E2.23.11.0", {"position": v(622.3, 317.5) * mm});
            skPoint(sketch, "E2.23.12.0", {"position": v(622.3, 342.9) * mm});
            skPoint(sketch, "E2.23.13.0", {"position": v(622.3, 368.3) * mm});
            skPoint(sketch, "E2.23.14.0", {"position": v(622.3, 393.7) * mm});
            skPoint(sketch, "E2.23.15.0", {"position": v(622.3, 419.1) * mm});
            skPoint(sketch, "E2.23.16.0", {"position": v(622.3, 444.5) * mm});
            skPoint(sketch, "E2.23.17.0", {"position": v(622.3, 469.9) * mm});
            skPoint(sketch, "E2.23.18.0", {"position": v(622.3, 495.3) * mm});
            skPoint(sketch, "E2.23.19.0", {"position": v(622.3, 520.7) * mm});
            skPoint(sketch, "E2.23.20.0", {"position": v(622.3, 546.1) * mm});
            skPoint(sketch, "E2.23.21.0", {"position": v(622.3, 571.5) * mm});
            skPoint(sketch, "E2.23.22.0", {"position": v(622.3, 596.9) * mm});
            skPoint(sketch, "E2.23.23.0", {"position": v(622.3, 622.3) * mm});
            skPoint(sketch, "E2.23.24.0", {"position": v(622.3, 647.7) * mm});
            skPoint(sketch, "E2.24.0.0", {"position": v(647.7, 38.1) * mm});
            skPoint(sketch, "E2.24.1.0", {"position": v(647.7, 63.5) * mm});
            skPoint(sketch, "E2.24.2.0", {"position": v(647.7, 88.9) * mm});
            skPoint(sketch, "E2.24.3.0", {"position": v(647.7, 114.3) * mm});
            skPoint(sketch, "E2.24.4.0", {"position": v(647.7, 139.7) * mm});
            skPoint(sketch, "E2.24.5.0", {"position": v(647.7, 165.1) * mm});
            skPoint(sketch, "E2.24.6.0", {"position": v(647.7, 190.5) * mm});
            skPoint(sketch, "E2.24.7.0", {"position": v(647.7, 215.9) * mm});
            skPoint(sketch, "E2.24.8.0", {"position": v(647.7, 241.3) * mm});
            skPoint(sketch, "E2.24.9.0", {"position": v(647.7, 266.7) * mm});
            skPoint(sketch, "E2.24.10.0", {"position": v(647.7, 292.1) * mm});
            skPoint(sketch, "E2.24.11.0", {"position": v(647.7, 317.5) * mm});
            skPoint(sketch, "E2.24.12.0", {"position": v(647.7, 342.9) * mm});
            skPoint(sketch, "E2.24.13.0", {"position": v(647.7, 368.3) * mm});
            skPoint(sketch, "E2.24.14.0", {"position": v(647.7, 393.7) * mm});
            skPoint(sketch, "E2.24.15.0", {"position": v(647.7, 419.1) * mm});
            skPoint(sketch, "E2.24.16.0", {"position": v(647.7, 444.5) * mm});
            skPoint(sketch, "E2.24.17.0", {"position": v(647.7, 469.9) * mm});
            skPoint(sketch, "E2.24.18.0", {"position": v(647.7, 495.3) * mm});
            skPoint(sketch, "E2.24.19.0", {"position": v(647.7, 520.7) * mm});
            skPoint(sketch, "E2.24.20.0", {"position": v(647.7, 546.1) * mm});
            skPoint(sketch, "E2.24.21.0", {"position": v(647.7, 571.5) * mm});
            skPoint(sketch, "E2.24.22.0", {"position": v(647.7, 596.9) * mm});
            skPoint(sketch, "E2.24.23.0", {"position": v(647.7, 622.3) * mm});
            skPoint(sketch, "E2.24.24.0", {"position": v(647.7, 647.7) * mm});
            skLineSegment(sketch, "E2.direction1", {"start": v(38.1, 38.1) * mm, "end": v(63.5, 38.1) * mm, "construction": true});
            skLineSegment(sketch, "E2.direction2", {"start": v(38.1, 38.1) * mm, "end": v(38.1, 63.5) * mm, "construction": true});
            skSolve(sketch);
        }
        {
            var Q0;
            Q0=makeQuery(id+"F0.imprint","IMPRINT",FACE,{"disambiguationData":[TD([[makeQuery(id+"F0.imprint","IMPRINT",EDGE,{"derivedFrom":sQuery(id+"F0.wireOp",EDGE,"E0.bottom")}),-1.0]])]});
            extrude(context, id + "F1", {"entities" : qUnion([Q0]), "depth" : 6.35 * mm});
        }
        {
            var Q0;
            Q0=sQuery(id+"F0.wireOp",VERTEX,"E2.9.5.0");
            var Q1;
            Q1=sQuery(id+"F0.wireOp",VERTEX,"E2.4.9.0");
            var Q2;
            Q2=sQuery(id+"F0.wireOp",VERTEX,"E2.2.5.0");
            var Q3;
            Q3=sQuery(id+"F0.wireOp",VERTEX,"E2.0.7.0");
            var Q4;
            Q4=sQuery(id+"F0.wireOp",VERTEX,"E2.4.3.0");
            var Q5;
            Q5=sQuery(id+"F0.wireOp",VERTEX,"E2.7.8.0");
            var Q6;
            Q6=sQuery(id+"F0.wireOp",VERTEX,"E2.6.1.0");
            var Q7;
            Q7=sQuery(id+"F0.wireOp",VERTEX,"E2.9.6.0");
            var Q8;
            Q8=sQuery(id+"F0.wireOp",VERTEX,"E2.2.6.0");
            var Q9;
            Q9=sQuery(id+"F0.wireOp",VERTEX,"E2.0.8.0");
            var Q10;
            Q10=sQuery(id+"F0.wireOp",VERTEX,"E2.4.4.0");
            var Q11;
            Q11=sQuery(id+"F0.wireOp",VERTEX,"E2.7.9.0");
            var Q12;
            Q12=sQuery(id+"F0.wireOp",VERTEX,"E2.6.2.0");
            var Q13;
            Q13=sQuery(id+"F0.wireOp",VERTEX,"E2.9.7.0");
            var Q14;
            Q14=sQuery(id+"F0.wireOp",VERTEX,"E2.8.0.0");
            var Q15;
            Q15=sQuery(id+"F0.wireOp",VERTEX,"E2.2.7.0");
            var Q16;
            Q16=sQuery(id+"F0.wireOp",VERTEX,"E2.1.0.0");
            var Q17;
            Q17=sQuery(id+"F0.wireOp",VERTEX,"E2.0.9.0");
            var Q18;
            Q18=sQuery(id+"F0.wireOp",VERTEX,"E2.4.5.0");
            var Q19;
            Q19=sQuery(id+"F0.wireOp",VERTEX,"E2.6.3.0");
            var Q20;
            Q20=sQuery(id+"F0.wireOp",VERTEX,"E2.9.8.0");
            var Q21;
            Q21=sQuery(id+"F0.wireOp",VERTEX,"E2.8.1.0");
            var Q22;
            Q22=sQuery(id+"F0.wireOp",VERTEX,"E2.2.8.0");
            var Q23;
            Q23=sQuery(id+"F0.wireOp",VERTEX,"E2.1.1.0");
            var Q24;
            Q24=sQuery(id+"F0.wireOp",VERTEX,"E2.4.6.0");
            var Q25;
            Q25=sQuery(id+"F0.wireOp",VERTEX,"E2.6.4.0");
            var Q26;
            Q26=sQuery(id+"F0.wireOp",VERTEX,"E2.9.9.0");
            var Q27;
            Q27=sQuery(id+"F0.wireOp",VERTEX,"E2.8.2.0");
            var Q28;
            Q28=sQuery(id+"F0.wireOp",VERTEX,"E2.6.5.0");
            var Q29;
            Q29=sQuery(id+"F0.wireOp",VERTEX,"E2.4.7.0");
            var Q30;
            Q30=sQuery(id+"F0.wireOp",VERTEX,"E2.8.3.0");
            var Q31;
            Q31=sQuery(id+"F0.wireOp",VERTEX,"E2.1.2.0");
            var Q32;
            Q32=sQuery(id+"F0.wireOp",VERTEX,"E2.3.0.0");
            var Q33;
            Q33=sQuery(id+"F0.wireOp",VERTEX,"E2.2.9.0");
            var Q34;
            Q34=sQuery(id+"F0.wireOp",VERTEX,"E2.8.4.0");
            var Q35;
            Q35=sQuery(id+"F0.wireOp",VERTEX,"E2.1.3.0");
            var Q36;
            Q36=sQuery(id+"F0.wireOp",VERTEX,"E2.3.1.0");
            var Q37;
            Q37=sQuery(id+"F0.wireOp",VERTEX,"E2.6.6.0");
            var Q38;
            Q38=sQuery(id+"F0.wireOp",VERTEX,"E2.4.8.0");
            var Q39;
            Q39=sQuery(id+"F0.wireOp",VERTEX,"E2.1.4.0");
            var Q40;
            Q40=sQuery(id+"F0.wireOp",VERTEX,"E2.3.2.0");
            var Q41;
            Q41=sQuery(id+"F0.wireOp",VERTEX,"E2.5.0.0");
            var Q42;
            Q42=sQuery(id+"F0.wireOp",VERTEX,"E2.8.5.0");
            var Q43;
            Q43=sQuery(id+"F0.wireOp",VERTEX,"E2.1.5.0");
            var Q44;
            Q44=sQuery(id+"F0.wireOp",VERTEX,"E2.3.3.0");
            var Q45;
            Q45=sQuery(id+"F0.wireOp",VERTEX,"E2.6.8.0");
            var Q46;
            Q46=sQuery(id+"F0.wireOp",VERTEX,"E2.5.1.0");
            var Q47;
            Q47=sQuery(id+"F0.wireOp",VERTEX,"E2.8.6.0");
            var Q48;
            Q48=sQuery(id+"F0.wireOp",VERTEX,"E2.1.8.0");
            var Q49;
            Q49=sQuery(id+"F0.wireOp",VERTEX,"E2.3.6.0");
            var Q50;
            Q50=sQuery(id+"F0.wireOp",VERTEX,"E2.7.2.0");
            var Q51;
            Q51=sQuery(id+"F0.wireOp",VERTEX,"E2.5.4.0");
            var Q52;
            Q52=sQuery(id+"F0.wireOp",VERTEX,"E2.9.0.0");
            var Q53;
            Q53=sQuery(id+"F0.wireOp",VERTEX,"E2.8.9.0");
            var Q54;
            Q54=sQuery(id+"F0.wireOp",VERTEX,"E2.1.6.0");
            var Q55;
            Q55=sQuery(id+"F0.wireOp",VERTEX,"E2.3.4.0");
            var Q56;
            Q56=sQuery(id+"F0.wireOp",VERTEX,"E2.6.9.0");
            var Q57;
            Q57=sQuery(id+"F0.wireOp",VERTEX,"E2.5.2.0");
            var Q58;
            Q58=sQuery(id+"F0.wireOp",VERTEX,"E2.8.7.0");
            var Q59;
            Q59=sQuery(id+"F0.wireOp",VERTEX,"E2.7.0.0");
            var Q60;
            Q60=sQuery(id+"F0.wireOp",VERTEX,"E2.2.0.0");
            var Q61;
            Q61=sQuery(id+"F0.wireOp",VERTEX,"E2.1.9.0");
            var Q62;
            Q62=sQuery(id+"F0.wireOp",VERTEX,"E2.3.7.0");
            var Q63;
            Q63=sQuery(id+"F0.wireOp",VERTEX,"E2.7.3.0");
            var Q64;
            Q64=sQuery(id+"F0.wireOp",VERTEX,"E2.5.5.0");
            var Q65;
            Q65=sQuery(id+"F0.wireOp",VERTEX,"E2.9.1.0");
            var Q66;
            Q66=sQuery(id+"F0.wireOp",VERTEX,"E2.1.7.0");
            var Q67;
            Q67=sQuery(id+"F0.wireOp",VERTEX,"E2.3.5.0");
            var Q68;
            Q68=sQuery(id+"F0.wireOp",VERTEX,"E2.5.3.0");
            var Q69;
            Q69=sQuery(id+"F0.wireOp",VERTEX,"E2.8.8.0");
            var Q70;
            Q70=sQuery(id+"F0.wireOp",VERTEX,"E2.7.1.0");
            var Q71;
            Q71=sQuery(id+"F0.wireOp",VERTEX,"E2.2.1.0");
            var Q72;
            Q72=sQuery(id+"F0.wireOp",VERTEX,"E2.3.8.0");
            var Q73;
            Q73=sQuery(id+"F0.wireOp",VERTEX,"E2.7.4.0");
            var Q74;
            Q74=sQuery(id+"F0.wireOp",VERTEX,"E2.5.6.0");
            var Q75;
            Q75=sQuery(id+"F0.wireOp",VERTEX,"E2.9.2.0");
            var Q76;
            Q76=sQuery(id+"F0.wireOp",VERTEX,"E2.0.1.0");
            var Q77;
            Q77=sQuery(id+"F0.wireOp",VERTEX,"E2.0.2.0");
            var Q78;
            Q78=sQuery(id+"F0.wireOp",VERTEX,"E2.0.3.0");
            var Q79;
            Q79=sQuery(id+"F0.wireOp",VERTEX,"E2.2.2.0");
            var Q80;
            Q80=sQuery(id+"F0.wireOp",VERTEX,"E2.0.4.0");
            var Q81;
            Q81=sQuery(id+"F0.wireOp",VERTEX,"E2.direction2.start");
            var Q82;
            Q82=sQuery(id+"F0.wireOp",VERTEX,"E2.4.0.0");
            var Q83;
            Q83=sQuery(id+"F0.wireOp",VERTEX,"E2.3.9.0");
            var Q84;
            Q84=sQuery(id+"F0.wireOp",VERTEX,"E2.7.5.0");
            var Q85;
            Q85=sQuery(id+"F0.wireOp",VERTEX,"E2.5.7.0");
            var Q86;
            Q86=sQuery(id+"F0.wireOp",VERTEX,"E2.9.3.0");
            var Q87;
            Q87=sQuery(id+"F0.wireOp",VERTEX,"E2.2.3.0");
            var Q88;
            Q88=sQuery(id+"F0.wireOp",VERTEX,"E2.0.5.0");
            var Q89;
            Q89=sQuery(id+"F0.wireOp",VERTEX,"E2.4.1.0");
            var Q90;
            Q90=sQuery(id+"F0.wireOp",VERTEX,"E2.7.6.0");
            var Q91;
            Q91=sQuery(id+"F0.wireOp",VERTEX,"E2.5.8.0");
            var Q92;
            Q92=sQuery(id+"F0.wireOp",VERTEX,"E2.9.4.0");
            var Q93;
            Q93=sQuery(id+"F0.wireOp",VERTEX,"E2.2.4.0");
            var Q94;
            Q94=sQuery(id+"F0.wireOp",VERTEX,"E2.0.6.0");
            var Q95;
            Q95=sQuery(id+"F0.wireOp",VERTEX,"E2.4.2.0");
            var Q96;
            Q96=sQuery(id+"F0.wireOp",VERTEX,"E2.7.7.0");
            var Q97;
            Q97=sQuery(id+"F0.wireOp",VERTEX,"E2.6.0.0");
            var Q98;
            Q98=sQuery(id+"F0.wireOp",VERTEX,"E2.5.9.0");
            var Q99;
            Q99=sQuery(id+"F0.wireOp",VERTEX,"E2.6.7.0");
            var Q100;
            Q100=makeQuery(id+"F1.opExtrude","SWEPT_BODY",BODY,{"disambiguationData":[OSD([sQuery(id+"F0.wireOp",EDGE,"E0.bottom"),sQuery(id+"F0.wireOp",EDGE,"E0.top"),sQuery(id+"F0.wireOp",EDGE,"E0.left"),sQuery(id+"F0.wireOp",EDGE,"E0.right")])]});
            hole(context, id + "F2", {"style" : HoleStyle.SIMPLE, "endStyle" : HoleEndStyle.THROUGH, "oppositeDirection" : true, "standardTappedOrClearance" : lookupTablePath({ "standard" : "ANSI", "fit" : "Close", "size" : "1/4", "type" : "Clearance" }), "standardBlindInLast" : lookupTablePath({ "fit" : "Close", "standard" : "ANSI", "size" : "1/4", "type" : "Clearance" }), "holeDiameter" : 6.53 * mm, "isTappedThrough" : true, "tappedDepth" : 12.7 * mm, "tapClearance" : 3, "startFromSketch" : true, "locations" : qUnion([Q0, Q1, Q2, Q3, Q4, Q5, Q6, Q7, Q8, Q9, Q10, Q11, Q12, Q13, Q14, Q15, Q16, Q17, Q18, Q19, Q20, Q21, Q22, Q23, Q24, Q25, Q26, Q27, Q28, Q29, Q30, Q31, Q32, Q33, Q34, Q35, Q36, Q37, Q38, Q39, Q40, Q41, Q42, Q43, Q44, Q45, Q46, Q47, Q48, Q49, Q50, Q51, Q52, Q53, Q54, Q55, Q56, Q57, Q58, Q59, Q60, Q61, Q62, Q63, Q64, Q65, Q66, Q67, Q68, Q69, Q70, Q71, Q72, Q73, Q74, Q75, Q76, Q77, Q78, Q79, Q80, Q81, Q82, Q83, Q84, Q85, Q86, Q87, Q88, Q89, Q90, Q91, Q92, Q93, Q94, Q95, Q96, Q97, Q98, Q99]), "scope" : qUnion([Q100])});
        }
        {
            var Q0;
            Q0=sQuery(id+"F0.wireOp",VERTEX,"E2.8.14.0");
            var Q1;
            Q1=sQuery(id+"F0.wireOp",VERTEX,"E2.7.14.0");
            var Q2;
            Q2=sQuery(id+"F0.wireOp",VERTEX,"E2.2.11.0");
            var Q3;
            Q3=sQuery(id+"F0.wireOp",VERTEX,"E2.1.14.0");
            var Q4;
            Q4=sQuery(id+"F0.wireOp",VERTEX,"E2.4.19.0");
            var Q5;
            Q5=sQuery(id+"F0.wireOp",VERTEX,"E2.3.12.0");
            var Q6;
            Q6=sQuery(id+"F0.wireOp",VERTEX,"E2.6.17.0");
            var Q7;
            Q7=sQuery(id+"F0.wireOp",VERTEX,"E2.5.10.0");
            var Q8;
            Q8=sQuery(id+"F0.wireOp",VERTEX,"E2.8.15.0");
            var Q9;
            Q9=sQuery(id+"F0.wireOp",VERTEX,"E2.1.15.0");
            var Q10;
            Q10=sQuery(id+"F0.wireOp",VERTEX,"E2.3.13.0");
            var Q11;
            Q11=sQuery(id+"F0.wireOp",VERTEX,"E2.6.18.0");
            var Q12;
            Q12=sQuery(id+"F0.wireOp",VERTEX,"E2.5.11.0");
            var Q13;
            Q13=sQuery(id+"F0.wireOp",VERTEX,"E2.8.16.0");
            var Q14;
            Q14=sQuery(id+"F0.wireOp",VERTEX,"E2.1.16.0");
            var Q15;
            Q15=sQuery(id+"F0.wireOp",VERTEX,"E2.3.14.0");
            var Q16;
            Q16=sQuery(id+"F0.wireOp",VERTEX,"E2.7.10.0");
            var Q17;
            Q17=sQuery(id+"F0.wireOp",VERTEX,"E2.6.19.0");
            var Q18;
            Q18=sQuery(id+"F0.wireOp",VERTEX,"E2.5.12.0");
            var Q19;
            Q19=sQuery(id+"F0.wireOp",VERTEX,"E2.8.17.0");
            var Q20;
            Q20=sQuery(id+"F0.wireOp",VERTEX,"E2.1.17.0");
            var Q21;
            Q21=sQuery(id+"F0.wireOp",VERTEX,"E2.0.10.0");
            var Q22;
            Q22=sQuery(id+"F0.wireOp",VERTEX,"E2.3.15.0");
            var Q23;
            Q23=sQuery(id+"F0.wireOp",VERTEX,"E2.7.11.0");
            var Q24;
            Q24=sQuery(id+"F0.wireOp",VERTEX,"E2.5.13.0");
            var Q25;
            Q25=sQuery(id+"F0.wireOp",VERTEX,"E2.8.18.0");
            var Q26;
            Q26=sQuery(id+"F0.wireOp",VERTEX,"E2.5.14.0");
            var Q27;
            Q27=sQuery(id+"F0.wireOp",VERTEX,"E2.8.19.0");
            var Q28;
            Q28=sQuery(id+"F0.wireOp",VERTEX,"E2.7.12.0");
            var Q29;
            Q29=sQuery(id+"F0.wireOp",VERTEX,"E2.9.10.0");
            var Q30;
            Q30=sQuery(id+"F0.wireOp",VERTEX,"E2.0.11.0");
            var Q31;
            Q31=sQuery(id+"F0.wireOp",VERTEX,"E2.3.16.0");
            var Q32;
            Q32=sQuery(id+"F0.wireOp",VERTEX,"E2.1.18.0");
            var Q33;
            Q33=sQuery(id+"F0.wireOp",VERTEX,"E2.7.13.0");
            var Q34;
            Q34=sQuery(id+"F0.wireOp",VERTEX,"E2.9.11.0");
            var Q35;
            Q35=sQuery(id+"F0.wireOp",VERTEX,"E2.0.12.0");
            var Q36;
            Q36=sQuery(id+"F0.wireOp",VERTEX,"E2.3.17.0");
            var Q37;
            Q37=sQuery(id+"F0.wireOp",VERTEX,"E2.2.10.0");
            var Q38;
            Q38=sQuery(id+"F0.wireOp",VERTEX,"E2.1.19.0");
            var Q39;
            Q39=sQuery(id+"F0.wireOp",VERTEX,"E2.5.15.0");
            var Q40;
            Q40=sQuery(id+"F0.wireOp",VERTEX,"E2.9.12.0");
            var Q41;
            Q41=sQuery(id+"F0.wireOp",VERTEX,"E2.0.13.0");
            var Q42;
            Q42=sQuery(id+"F0.wireOp",VERTEX,"E2.3.18.0");
            var Q43;
            Q43=sQuery(id+"F0.wireOp",VERTEX,"E2.5.16.0");
            var Q44;
            Q44=sQuery(id+"F0.wireOp",VERTEX,"E2.0.14.0");
            var Q45;
            Q45=sQuery(id+"F0.wireOp",VERTEX,"E2.3.19.0");
            var Q46;
            Q46=sQuery(id+"F0.wireOp",VERTEX,"E2.2.12.0");
            var Q47;
            Q47=sQuery(id+"F0.wireOp",VERTEX,"E2.5.17.0");
            var Q48;
            Q48=sQuery(id+"F0.wireOp",VERTEX,"E2.4.10.0");
            var Q49;
            Q49=sQuery(id+"F0.wireOp",VERTEX,"E2.7.15.0");
            var Q50;
            Q50=sQuery(id+"F0.wireOp",VERTEX,"E2.9.13.0");
            var Q51;
            Q51=sQuery(id+"F0.wireOp",VERTEX,"E2.0.17.0");
            var Q52;
            Q52=sQuery(id+"F0.wireOp",VERTEX,"E2.4.13.0");
            var Q53;
            Q53=sQuery(id+"F0.wireOp",VERTEX,"E2.2.15.0");
            var Q54;
            Q54=sQuery(id+"F0.wireOp",VERTEX,"E2.6.11.0");
            var Q55;
            Q55=sQuery(id+"F0.wireOp",VERTEX,"E2.9.16.0");
            var Q56;
            Q56=sQuery(id+"F0.wireOp",VERTEX,"E2.7.18.0");
            var Q57;
            Q57=sQuery(id+"F0.wireOp",VERTEX,"E2.0.15.0");
            var Q58;
            Q58=sQuery(id+"F0.wireOp",VERTEX,"E2.2.13.0");
            var Q59;
            Q59=sQuery(id+"F0.wireOp",VERTEX,"E2.5.18.0");
            var Q60;
            Q60=sQuery(id+"F0.wireOp",VERTEX,"E2.4.11.0");
            var Q61;
            Q61=sQuery(id+"F0.wireOp",VERTEX,"E2.7.16.0");
            var Q62;
            Q62=sQuery(id+"F0.wireOp",VERTEX,"E2.9.14.0");
            var Q63;
            Q63=sQuery(id+"F0.wireOp",VERTEX,"E2.0.18.0");
            var Q64;
            Q64=sQuery(id+"F0.wireOp",VERTEX,"E2.4.14.0");
            var Q65;
            Q65=sQuery(id+"F0.wireOp",VERTEX,"E2.2.16.0");
            var Q66;
            Q66=sQuery(id+"F0.wireOp",VERTEX,"E2.6.12.0");
            var Q67;
            Q67=sQuery(id+"F0.wireOp",VERTEX,"E2.9.17.0");
            var Q68;
            Q68=sQuery(id+"F0.wireOp",VERTEX,"E2.8.10.0");
            var Q69;
            Q69=sQuery(id+"F0.wireOp",VERTEX,"E2.7.19.0");
            var Q70;
            Q70=sQuery(id+"F0.wireOp",VERTEX,"E2.0.16.0");
            var Q71;
            Q71=sQuery(id+"F0.wireOp",VERTEX,"E2.2.14.0");
            var Q72;
            Q72=sQuery(id+"F0.wireOp",VERTEX,"E2.6.10.0");
            var Q73;
            Q73=sQuery(id+"F0.wireOp",VERTEX,"E2.5.19.0");
            var Q74;
            Q74=sQuery(id+"F0.wireOp",VERTEX,"E2.4.12.0");
            var Q75;
            Q75=sQuery(id+"F0.wireOp",VERTEX,"E2.7.17.0");
            var Q76;
            Q76=sQuery(id+"F0.wireOp",VERTEX,"E2.9.15.0");
            var Q77;
            Q77=sQuery(id+"F0.wireOp",VERTEX,"E2.1.10.0");
            var Q78;
            Q78=sQuery(id+"F0.wireOp",VERTEX,"E2.0.19.0");
            var Q79;
            Q79=sQuery(id+"F0.wireOp",VERTEX,"E2.4.15.0");
            var Q80;
            Q80=sQuery(id+"F0.wireOp",VERTEX,"E2.2.17.0");
            var Q81;
            Q81=sQuery(id+"F0.wireOp",VERTEX,"E2.6.13.0");
            var Q82;
            Q82=sQuery(id+"F0.wireOp",VERTEX,"E2.9.18.0");
            var Q83;
            Q83=sQuery(id+"F0.wireOp",VERTEX,"E2.8.11.0");
            var Q84;
            Q84=sQuery(id+"F0.wireOp",VERTEX,"E2.1.11.0");
            var Q85;
            Q85=sQuery(id+"F0.wireOp",VERTEX,"E2.4.16.0");
            var Q86;
            Q86=sQuery(id+"F0.wireOp",VERTEX,"E2.2.18.0");
            var Q87;
            Q87=sQuery(id+"F0.wireOp",VERTEX,"E2.6.14.0");
            var Q88;
            Q88=sQuery(id+"F0.wireOp",VERTEX,"E2.9.19.0");
            var Q89;
            Q89=sQuery(id+"F0.wireOp",VERTEX,"E2.8.12.0");
            var Q90;
            Q90=sQuery(id+"F0.wireOp",VERTEX,"E2.1.12.0");
            var Q91;
            Q91=sQuery(id+"F0.wireOp",VERTEX,"E2.4.17.0");
            var Q92;
            Q92=sQuery(id+"F0.wireOp",VERTEX,"E2.3.10.0");
            var Q93;
            Q93=sQuery(id+"F0.wireOp",VERTEX,"E2.2.19.0");
            var Q94;
            Q94=sQuery(id+"F0.wireOp",VERTEX,"E2.6.15.0");
            var Q95;
            Q95=sQuery(id+"F0.wireOp",VERTEX,"E2.8.13.0");
            var Q96;
            Q96=sQuery(id+"F0.wireOp",VERTEX,"E2.1.13.0");
            var Q97;
            Q97=sQuery(id+"F0.wireOp",VERTEX,"E2.4.18.0");
            var Q98;
            Q98=sQuery(id+"F0.wireOp",VERTEX,"E2.3.11.0");
            var Q99;
            Q99=sQuery(id+"F0.wireOp",VERTEX,"E2.6.16.0");
            var Q100;
            Q100=makeQuery(id+"F1.opExtrude","SWEPT_BODY",BODY,{"disambiguationData":[OSD([sQuery(id+"F0.wireOp",EDGE,"E0.bottom"),sQuery(id+"F0.wireOp",EDGE,"E0.top"),sQuery(id+"F0.wireOp",EDGE,"E0.left"),sQuery(id+"F0.wireOp",EDGE,"E0.right")])]});
            hole(context, id + "F3", {"style" : HoleStyle.SIMPLE, "endStyle" : HoleEndStyle.THROUGH, "oppositeDirection" : true, "standardTappedOrClearance" : lookupTablePath({ "standard" : "ANSI", "fit" : "Close", "size" : "1/4", "type" : "Clearance" }), "standardBlindInLast" : lookupTablePath({ "fit" : "Close", "standard" : "ANSI", "size" : "1/4", "type" : "Clearance" }), "holeDiameter" : 6.53 * mm, "isTappedThrough" : true, "tappedDepth" : 12.7 * mm, "tapClearance" : 3, "startFromSketch" : true, "locations" : qUnion([Q0, Q1, Q2, Q3, Q4, Q5, Q6, Q7, Q8, Q9, Q10, Q11, Q12, Q13, Q14, Q15, Q16, Q17, Q18, Q19, Q20, Q21, Q22, Q23, Q24, Q25, Q26, Q27, Q28, Q29, Q30, Q31, Q32, Q33, Q34, Q35, Q36, Q37, Q38, Q39, Q40, Q41, Q42, Q43, Q44, Q45, Q46, Q47, Q48, Q49, Q50, Q51, Q52, Q53, Q54, Q55, Q56, Q57, Q58, Q59, Q60, Q61, Q62, Q63, Q64, Q65, Q66, Q67, Q68, Q69, Q70, Q71, Q72, Q73, Q74, Q75, Q76, Q77, Q78, Q79, Q80, Q81, Q82, Q83, Q84, Q85, Q86, Q87, Q88, Q89, Q90, Q91, Q92, Q93, Q94, Q95, Q96, Q97, Q98, Q99]), "scope" : qUnion([Q100])});
        }
        {
            var Q0;
            Q0=sQuery(id+"F0.wireOp",VERTEX,"E2.11.3.0");
            var Q1;
            Q1=sQuery(id+"F0.wireOp",VERTEX,"E2.13.1.0");
            var Q2;
            Q2=sQuery(id+"F0.wireOp",VERTEX,"E2.14.8.0");
            var Q3;
            Q3=sQuery(id+"F0.wireOp",VERTEX,"E2.16.6.0");
            var Q4;
            Q4=sQuery(id+"F0.wireOp",VERTEX,"E2.11.4.0");
            var Q5;
            Q5=sQuery(id+"F0.wireOp",VERTEX,"E2.15.0.0");
            var Q6;
            Q6=sQuery(id+"F0.wireOp",VERTEX,"E2.14.9.0");
            var Q7;
            Q7=sQuery(id+"F0.wireOp",VERTEX,"E2.13.2.0");
            var Q8;
            Q8=sQuery(id+"F0.wireOp",VERTEX,"E2.16.7.0");
            var Q9;
            Q9=sQuery(id+"F0.wireOp",VERTEX,"E2.18.5.0");
            var Q10;
            Q10=sQuery(id+"F0.wireOp",VERTEX,"E2.11.5.0");
            var Q11;
            Q11=sQuery(id+"F0.wireOp",VERTEX,"E2.15.1.0");
            var Q12;
            Q12=sQuery(id+"F0.wireOp",VERTEX,"E2.13.3.0");
            var Q13;
            Q13=sQuery(id+"F0.wireOp",VERTEX,"E2.16.8.0");
            var Q14;
            Q14=sQuery(id+"F0.wireOp",VERTEX,"E2.18.6.0");
            var Q15;
            Q15=sQuery(id+"F0.wireOp",VERTEX,"E2.11.6.0");
            var Q16;
            Q16=sQuery(id+"F0.wireOp",VERTEX,"E2.15.2.0");
            var Q17;
            Q17=sQuery(id+"F0.wireOp",VERTEX,"E2.13.4.0");
            var Q18;
            Q18=sQuery(id+"F0.wireOp",VERTEX,"E2.16.9.0");
            var Q19;
            Q19=sQuery(id+"F0.wireOp",VERTEX,"E2.18.7.0");
            var Q20;
            Q20=sQuery(id+"F0.wireOp",VERTEX,"E2.17.0.0");
            var Q21;
            Q21=sQuery(id+"F0.wireOp",VERTEX,"E2.10.0.0");
            var Q22;
            Q22=sQuery(id+"F0.wireOp",VERTEX,"E2.11.7.0");
            var Q23;
            Q23=sQuery(id+"F0.wireOp",VERTEX,"E2.15.3.0");
            var Q24;
            Q24=sQuery(id+"F0.wireOp",VERTEX,"E2.13.5.0");
            var Q25;
            Q25=sQuery(id+"F0.wireOp",VERTEX,"E2.18.8.0");
            var Q26;
            Q26=sQuery(id+"F0.wireOp",VERTEX,"E2.17.1.0");
            var Q27;
            Q27=sQuery(id+"F0.wireOp",VERTEX,"E2.11.8.0");
            var Q28;
            Q28=sQuery(id+"F0.wireOp",VERTEX,"E2.10.1.0");
            var Q29;
            Q29=sQuery(id+"F0.wireOp",VERTEX,"E2.13.6.0");
            var Q30;
            Q30=sQuery(id+"F0.wireOp",VERTEX,"E2.15.4.0");
            var Q31;
            Q31=sQuery(id+"F0.wireOp",VERTEX,"E2.17.2.0");
            var Q32;
            Q32=sQuery(id+"F0.wireOp",VERTEX,"E2.19.0.0");
            var Q33;
            Q33=sQuery(id+"F0.wireOp",VERTEX,"E2.18.9.0");
            var Q34;
            Q34=sQuery(id+"F0.wireOp",VERTEX,"E2.11.9.0");
            var Q35;
            Q35=sQuery(id+"F0.wireOp",VERTEX,"E2.10.2.0");
            var Q36;
            Q36=sQuery(id+"F0.wireOp",VERTEX,"E2.13.7.0");
            var Q37;
            Q37=sQuery(id+"F0.wireOp",VERTEX,"E2.12.0.0");
            var Q38;
            Q38=sQuery(id+"F0.wireOp",VERTEX,"E2.15.5.0");
            var Q39;
            Q39=sQuery(id+"F0.wireOp",VERTEX,"E2.17.3.0");
            var Q40;
            Q40=sQuery(id+"F0.wireOp",VERTEX,"E2.19.1.0");
            var Q41;
            Q41=sQuery(id+"F0.wireOp",VERTEX,"E2.10.3.0");
            var Q42;
            Q42=sQuery(id+"F0.wireOp",VERTEX,"E2.13.8.0");
            var Q43;
            Q43=sQuery(id+"F0.wireOp",VERTEX,"E2.12.1.0");
            var Q44;
            Q44=sQuery(id+"F0.wireOp",VERTEX,"E2.15.6.0");
            var Q45;
            Q45=sQuery(id+"F0.wireOp",VERTEX,"E2.17.4.0");
            var Q46;
            Q46=sQuery(id+"F0.wireOp",VERTEX,"E2.19.2.0");
            var Q47;
            Q47=sQuery(id+"F0.wireOp",VERTEX,"E2.18.4.0");
            var Q48;
            Q48=sQuery(id+"F0.wireOp",VERTEX,"E2.14.0.0");
            var Q49;
            Q49=sQuery(id+"F0.wireOp",VERTEX,"E2.13.9.0");
            var Q50;
            Q50=sQuery(id+"F0.wireOp",VERTEX,"E2.12.2.0");
            var Q51;
            Q51=sQuery(id+"F0.wireOp",VERTEX,"E2.15.7.0");
            var Q52;
            Q52=sQuery(id+"F0.wireOp",VERTEX,"E2.17.5.0");
            var Q53;
            Q53=sQuery(id+"F0.wireOp",VERTEX,"E2.19.3.0");
            var Q54;
            Q54=sQuery(id+"F0.wireOp",VERTEX,"E2.10.4.0");
            var Q55;
            Q55=sQuery(id+"F0.wireOp",VERTEX,"E2.12.5.0");
            var Q56;
            Q56=sQuery(id+"F0.wireOp",VERTEX,"E2.10.7.0");
            var Q57;
            Q57=sQuery(id+"F0.wireOp",VERTEX,"E2.15.8.0");
            var Q58;
            Q58=sQuery(id+"F0.wireOp",VERTEX,"E2.17.6.0");
            var Q59;
            Q59=sQuery(id+"F0.wireOp",VERTEX,"E2.19.4.0");
            var Q60;
            Q60=sQuery(id+"F0.wireOp",VERTEX,"E2.14.3.0");
            var Q61;
            Q61=sQuery(id+"F0.wireOp",VERTEX,"E2.16.1.0");
            var Q62;
            Q62=sQuery(id+"F0.wireOp",VERTEX,"E2.17.8.0");
            var Q63;
            Q63=sQuery(id+"F0.wireOp",VERTEX,"E2.19.6.0");
            var Q64;
            Q64=sQuery(id+"F0.wireOp",VERTEX,"E2.10.5.0");
            var Q65;
            Q65=sQuery(id+"F0.wireOp",VERTEX,"E2.14.1.0");
            var Q66;
            Q66=sQuery(id+"F0.wireOp",VERTEX,"E2.12.3.0");
            var Q67;
            Q67=sQuery(id+"F0.wireOp",VERTEX,"E2.12.6.0");
            var Q68;
            Q68=sQuery(id+"F0.wireOp",VERTEX,"E2.10.8.0");
            var Q69;
            Q69=sQuery(id+"F0.wireOp",VERTEX,"E2.14.4.0");
            var Q70;
            Q70=sQuery(id+"F0.wireOp",VERTEX,"E2.17.7.0");
            var Q71;
            Q71=sQuery(id+"F0.wireOp",VERTEX,"E2.19.5.0");
            var Q72;
            Q72=sQuery(id+"F0.wireOp",VERTEX,"E2.16.2.0");
            var Q73;
            Q73=sQuery(id+"F0.wireOp",VERTEX,"E2.18.0.0");
            var Q74;
            Q74=sQuery(id+"F0.wireOp",VERTEX,"E2.17.9.0");
            var Q75;
            Q75=sQuery(id+"F0.wireOp",VERTEX,"E2.19.7.0");
            var Q76;
            Q76=sQuery(id+"F0.wireOp",VERTEX,"E2.10.6.0");
            var Q77;
            Q77=sQuery(id+"F0.wireOp",VERTEX,"E2.14.2.0");
            var Q78;
            Q78=sQuery(id+"F0.wireOp",VERTEX,"E2.12.4.0");
            var Q79;
            Q79=sQuery(id+"F0.wireOp",VERTEX,"E2.16.0.0");
            var Q80;
            Q80=sQuery(id+"F0.wireOp",VERTEX,"E2.15.9.0");
            var Q81;
            Q81=sQuery(id+"F0.wireOp",VERTEX,"E2.12.7.0");
            var Q82;
            Q82=sQuery(id+"F0.wireOp",VERTEX,"E2.11.0.0");
            var Q83;
            Q83=sQuery(id+"F0.wireOp",VERTEX,"E2.10.9.0");
            var Q84;
            Q84=sQuery(id+"F0.wireOp",VERTEX,"E2.14.5.0");
            var Q85;
            Q85=sQuery(id+"F0.wireOp",VERTEX,"E2.16.3.0");
            var Q86;
            Q86=sQuery(id+"F0.wireOp",VERTEX,"E2.18.1.0");
            var Q87;
            Q87=sQuery(id+"F0.wireOp",VERTEX,"E2.19.8.0");
            var Q88;
            Q88=sQuery(id+"F0.wireOp",VERTEX,"E2.19.9.0");
            var Q89;
            Q89=sQuery(id+"F0.wireOp",VERTEX,"E2.12.8.0");
            var Q90;
            Q90=sQuery(id+"F0.wireOp",VERTEX,"E2.11.1.0");
            var Q91;
            Q91=sQuery(id+"F0.wireOp",VERTEX,"E2.14.6.0");
            var Q92;
            Q92=sQuery(id+"F0.wireOp",VERTEX,"E2.16.4.0");
            var Q93;
            Q93=sQuery(id+"F0.wireOp",VERTEX,"E2.18.2.0");
            var Q94;
            Q94=sQuery(id+"F0.wireOp",VERTEX,"E2.12.9.0");
            var Q95;
            Q95=sQuery(id+"F0.wireOp",VERTEX,"E2.11.2.0");
            var Q96;
            Q96=sQuery(id+"F0.wireOp",VERTEX,"E2.14.7.0");
            var Q97;
            Q97=sQuery(id+"F0.wireOp",VERTEX,"E2.13.0.0");
            var Q98;
            Q98=sQuery(id+"F0.wireOp",VERTEX,"E2.16.5.0");
            var Q99;
            Q99=sQuery(id+"F0.wireOp",VERTEX,"E2.18.3.0");
            var Q100;
            Q100=makeQuery(id+"F1.opExtrude","SWEPT_BODY",BODY,{"disambiguationData":[OSD([sQuery(id+"F0.wireOp",EDGE,"E0.bottom"),sQuery(id+"F0.wireOp",EDGE,"E0.top"),sQuery(id+"F0.wireOp",EDGE,"E0.left"),sQuery(id+"F0.wireOp",EDGE,"E0.right")])]});
            hole(context, id + "F4", {"style" : HoleStyle.SIMPLE, "endStyle" : HoleEndStyle.THROUGH, "oppositeDirection" : true, "standardTappedOrClearance" : lookupTablePath({ "standard" : "ANSI", "fit" : "Close", "size" : "1/4", "type" : "Clearance" }), "standardBlindInLast" : lookupTablePath({ "fit" : "Close", "standard" : "ANSI", "size" : "1/4", "type" : "Clearance" }), "holeDiameter" : 6.53 * mm, "isTappedThrough" : true, "tappedDepth" : 12.7 * mm, "tapClearance" : 3, "startFromSketch" : true, "locations" : qUnion([Q0, Q1, Q2, Q3, Q4, Q5, Q6, Q7, Q8, Q9, Q10, Q11, Q12, Q13, Q14, Q15, Q16, Q17, Q18, Q19, Q20, Q21, Q22, Q23, Q24, Q25, Q26, Q27, Q28, Q29, Q30, Q31, Q32, Q33, Q34, Q35, Q36, Q37, Q38, Q39, Q40, Q41, Q42, Q43, Q44, Q45, Q46, Q47, Q48, Q49, Q50, Q51, Q52, Q53, Q54, Q55, Q56, Q57, Q58, Q59, Q60, Q61, Q62, Q63, Q64, Q65, Q66, Q67, Q68, Q69, Q70, Q71, Q72, Q73, Q74, Q75, Q76, Q77, Q78, Q79, Q80, Q81, Q82, Q83, Q84, Q85, Q86, Q87, Q88, Q89, Q90, Q91, Q92, Q93, Q94, Q95, Q96, Q97, Q98, Q99]), "scope" : qUnion([Q100])});
        }
        {
            var Q0;
            Q0=sQuery(id+"F0.wireOp",VERTEX,"E2.12.10.0");
            var Q1;
            Q1=sQuery(id+"F0.wireOp",VERTEX,"E2.11.19.0");
            var Q2;
            Q2=sQuery(id+"F0.wireOp",VERTEX,"E2.10.12.0");
            var Q3;
            Q3=sQuery(id+"F0.wireOp",VERTEX,"E2.13.17.0");
            var Q4;
            Q4=sQuery(id+"F0.wireOp",VERTEX,"E2.15.15.0");
            var Q5;
            Q5=sQuery(id+"F0.wireOp",VERTEX,"E2.19.11.0");
            var Q6;
            Q6=sQuery(id+"F0.wireOp",VERTEX,"E2.12.11.0");
            var Q7;
            Q7=sQuery(id+"F0.wireOp",VERTEX,"E2.10.13.0");
            var Q8;
            Q8=sQuery(id+"F0.wireOp",VERTEX,"E2.13.18.0");
            var Q9;
            Q9=sQuery(id+"F0.wireOp",VERTEX,"E2.15.16.0");
            var Q10;
            Q10=sQuery(id+"F0.wireOp",VERTEX,"E2.17.14.0");
            var Q11;
            Q11=sQuery(id+"F0.wireOp",VERTEX,"E2.19.12.0");
            var Q12;
            Q12=sQuery(id+"F0.wireOp",VERTEX,"E2.12.12.0");
            var Q13;
            Q13=sQuery(id+"F0.wireOp",VERTEX,"E2.10.14.0");
            var Q14;
            Q14=sQuery(id+"F0.wireOp",VERTEX,"E2.14.10.0");
            var Q15;
            Q15=sQuery(id+"F0.wireOp",VERTEX,"E2.13.19.0");
            var Q16;
            Q16=sQuery(id+"F0.wireOp",VERTEX,"E2.15.17.0");
            var Q17;
            Q17=sQuery(id+"F0.wireOp",VERTEX,"E2.17.15.0");
            var Q18;
            Q18=sQuery(id+"F0.wireOp",VERTEX,"E2.19.13.0");
            var Q19;
            Q19=sQuery(id+"F0.wireOp",VERTEX,"E2.12.13.0");
            var Q20;
            Q20=sQuery(id+"F0.wireOp",VERTEX,"E2.10.15.0");
            var Q21;
            Q21=sQuery(id+"F0.wireOp",VERTEX,"E2.14.11.0");
            var Q22;
            Q22=sQuery(id+"F0.wireOp",VERTEX,"E2.15.18.0");
            var Q23;
            Q23=sQuery(id+"F0.wireOp",VERTEX,"E2.17.16.0");
            var Q24;
            Q24=sQuery(id+"F0.wireOp",VERTEX,"E2.19.14.0");
            var Q25;
            Q25=sQuery(id+"F0.wireOp",VERTEX,"E2.12.14.0");
            var Q26;
            Q26=sQuery(id+"F0.wireOp",VERTEX,"E2.10.16.0");
            var Q27;
            Q27=sQuery(id+"F0.wireOp",VERTEX,"E2.14.12.0");
            var Q28;
            Q28=sQuery(id+"F0.wireOp",VERTEX,"E2.15.19.0");
            var Q29;
            Q29=sQuery(id+"F0.wireOp",VERTEX,"E2.16.10.0");
            var Q30;
            Q30=sQuery(id+"F0.wireOp",VERTEX,"E2.17.17.0");
            var Q31;
            Q31=sQuery(id+"F0.wireOp",VERTEX,"E2.19.15.0");
            var Q32;
            Q32=sQuery(id+"F0.wireOp",VERTEX,"E2.10.17.0");
            var Q33;
            Q33=sQuery(id+"F0.wireOp",VERTEX,"E2.12.15.0");
            var Q34;
            Q34=sQuery(id+"F0.wireOp",VERTEX,"E2.14.13.0");
            var Q35;
            Q35=sQuery(id+"F0.wireOp",VERTEX,"E2.17.18.0");
            var Q36;
            Q36=sQuery(id+"F0.wireOp",VERTEX,"E2.16.11.0");
            var Q37;
            Q37=sQuery(id+"F0.wireOp",VERTEX,"E2.19.16.0");
            var Q38;
            Q38=sQuery(id+"F0.wireOp",VERTEX,"E2.10.18.0");
            var Q39;
            Q39=sQuery(id+"F0.wireOp",VERTEX,"E2.12.16.0");
            var Q40;
            Q40=sQuery(id+"F0.wireOp",VERTEX,"E2.14.14.0");
            var Q41;
            Q41=sQuery(id+"F0.wireOp",VERTEX,"E2.17.19.0");
            var Q42;
            Q42=sQuery(id+"F0.wireOp",VERTEX,"E2.16.12.0");
            var Q43;
            Q43=sQuery(id+"F0.wireOp",VERTEX,"E2.19.17.0");
            var Q44;
            Q44=sQuery(id+"F0.wireOp",VERTEX,"E2.18.10.0");
            var Q45;
            Q45=sQuery(id+"F0.wireOp",VERTEX,"E2.11.10.0");
            var Q46;
            Q46=sQuery(id+"F0.wireOp",VERTEX,"E2.10.19.0");
            var Q47;
            Q47=sQuery(id+"F0.wireOp",VERTEX,"E2.12.17.0");
            var Q48;
            Q48=sQuery(id+"F0.wireOp",VERTEX,"E2.14.15.0");
            var Q49;
            Q49=sQuery(id+"F0.wireOp",VERTEX,"E2.16.13.0");
            var Q50;
            Q50=sQuery(id+"F0.wireOp",VERTEX,"E2.19.18.0");
            var Q51;
            Q51=sQuery(id+"F0.wireOp",VERTEX,"E2.18.11.0");
            var Q52;
            Q52=sQuery(id+"F0.wireOp",VERTEX,"E2.17.13.0");
            var Q53;
            Q53=sQuery(id+"F0.wireOp",VERTEX,"E2.12.18.0");
            var Q54;
            Q54=sQuery(id+"F0.wireOp",VERTEX,"E2.14.16.0");
            var Q55;
            Q55=sQuery(id+"F0.wireOp",VERTEX,"E2.16.14.0");
            var Q56;
            Q56=sQuery(id+"F0.wireOp",VERTEX,"E2.19.19.0");
            var Q57;
            Q57=sQuery(id+"F0.wireOp",VERTEX,"E2.18.12.0");
            var Q58;
            Q58=sQuery(id+"F0.wireOp",VERTEX,"E2.11.11.0");
            var Q59;
            Q59=sQuery(id+"F0.wireOp",VERTEX,"E2.11.14.0");
            var Q60;
            Q60=sQuery(id+"F0.wireOp",VERTEX,"E2.14.17.0");
            var Q61;
            Q61=sQuery(id+"F0.wireOp",VERTEX,"E2.16.15.0");
            var Q62;
            Q62=sQuery(id+"F0.wireOp",VERTEX,"E2.18.13.0");
            var Q63;
            Q63=sQuery(id+"F0.wireOp",VERTEX,"E2.14.19.0");
            var Q64;
            Q64=sQuery(id+"F0.wireOp",VERTEX,"E2.13.12.0");
            var Q65;
            Q65=sQuery(id+"F0.wireOp",VERTEX,"E2.15.10.0");
            var Q66;
            Q66=sQuery(id+"F0.wireOp",VERTEX,"E2.18.15.0");
            var Q67;
            Q67=sQuery(id+"F0.wireOp",VERTEX,"E2.16.17.0");
            var Q68;
            Q68=sQuery(id+"F0.wireOp",VERTEX,"E2.11.12.0");
            var Q69;
            Q69=sQuery(id+"F0.wireOp",VERTEX,"E2.13.10.0");
            var Q70;
            Q70=sQuery(id+"F0.wireOp",VERTEX,"E2.12.19.0");
            var Q71;
            Q71=sQuery(id+"F0.wireOp",VERTEX,"E2.11.15.0");
            var Q72;
            Q72=sQuery(id+"F0.wireOp",VERTEX,"E2.13.13.0");
            var Q73;
            Q73=sQuery(id+"F0.wireOp",VERTEX,"E2.16.16.0");
            var Q74;
            Q74=sQuery(id+"F0.wireOp",VERTEX,"E2.18.14.0");
            var Q75;
            Q75=sQuery(id+"F0.wireOp",VERTEX,"E2.15.11.0");
            var Q76;
            Q76=sQuery(id+"F0.wireOp",VERTEX,"E2.18.16.0");
            var Q77;
            Q77=sQuery(id+"F0.wireOp",VERTEX,"E2.16.18.0");
            var Q78;
            Q78=sQuery(id+"F0.wireOp",VERTEX,"E2.11.13.0");
            var Q79;
            Q79=sQuery(id+"F0.wireOp",VERTEX,"E2.13.11.0");
            var Q80;
            Q80=sQuery(id+"F0.wireOp",VERTEX,"E2.14.18.0");
            var Q81;
            Q81=sQuery(id+"F0.wireOp",VERTEX,"E2.11.16.0");
            var Q82;
            Q82=sQuery(id+"F0.wireOp",VERTEX,"E2.13.14.0");
            var Q83;
            Q83=sQuery(id+"F0.wireOp",VERTEX,"E2.15.12.0");
            var Q84;
            Q84=sQuery(id+"F0.wireOp",VERTEX,"E2.18.17.0");
            var Q85;
            Q85=sQuery(id+"F0.wireOp",VERTEX,"E2.17.10.0");
            var Q86;
            Q86=sQuery(id+"F0.wireOp",VERTEX,"E2.16.19.0");
            var Q87;
            Q87=sQuery(id+"F0.wireOp",VERTEX,"E2.11.17.0");
            var Q88;
            Q88=sQuery(id+"F0.wireOp",VERTEX,"E2.10.10.0");
            var Q89;
            Q89=sQuery(id+"F0.wireOp",VERTEX,"E2.13.15.0");
            var Q90;
            Q90=sQuery(id+"F0.wireOp",VERTEX,"E2.15.13.0");
            var Q91;
            Q91=sQuery(id+"F0.wireOp",VERTEX,"E2.18.18.0");
            var Q92;
            Q92=sQuery(id+"F0.wireOp",VERTEX,"E2.17.11.0");
            var Q93;
            Q93=sQuery(id+"F0.wireOp",VERTEX,"E2.11.18.0");
            var Q94;
            Q94=sQuery(id+"F0.wireOp",VERTEX,"E2.10.11.0");
            var Q95;
            Q95=sQuery(id+"F0.wireOp",VERTEX,"E2.13.16.0");
            var Q96;
            Q96=sQuery(id+"F0.wireOp",VERTEX,"E2.15.14.0");
            var Q97;
            Q97=sQuery(id+"F0.wireOp",VERTEX,"E2.18.19.0");
            var Q98;
            Q98=sQuery(id+"F0.wireOp",VERTEX,"E2.17.12.0");
            var Q99;
            Q99=sQuery(id+"F0.wireOp",VERTEX,"E2.19.10.0");
            var Q100;
            Q100=makeQuery(id+"F1.opExtrude","SWEPT_BODY",BODY,{"disambiguationData":[OSD([sQuery(id+"F0.wireOp",EDGE,"E0.bottom"),sQuery(id+"F0.wireOp",EDGE,"E0.top"),sQuery(id+"F0.wireOp",EDGE,"E0.left"),sQuery(id+"F0.wireOp",EDGE,"E0.right")])]});
            hole(context, id + "F5", {"style" : HoleStyle.SIMPLE, "endStyle" : HoleEndStyle.THROUGH, "oppositeDirection" : true, "standardTappedOrClearance" : lookupTablePath({ "standard" : "ANSI", "fit" : "Close", "size" : "1/4", "type" : "Clearance" }), "standardBlindInLast" : lookupTablePath({ "fit" : "Close", "standard" : "ANSI", "size" : "1/4", "type" : "Clearance" }), "holeDiameter" : 6.53 * mm, "isTappedThrough" : true, "tappedDepth" : 12.7 * mm, "tapClearance" : 3, "startFromSketch" : true, "locations" : qUnion([Q0, Q1, Q2, Q3, Q4, Q5, Q6, Q7, Q8, Q9, Q10, Q11, Q12, Q13, Q14, Q15, Q16, Q17, Q18, Q19, Q20, Q21, Q22, Q23, Q24, Q25, Q26, Q27, Q28, Q29, Q30, Q31, Q32, Q33, Q34, Q35, Q36, Q37, Q38, Q39, Q40, Q41, Q42, Q43, Q44, Q45, Q46, Q47, Q48, Q49, Q50, Q51, Q52, Q53, Q54, Q55, Q56, Q57, Q58, Q59, Q60, Q61, Q62, Q63, Q64, Q65, Q66, Q67, Q68, Q69, Q70, Q71, Q72, Q73, Q74, Q75, Q76, Q77, Q78, Q79, Q80, Q81, Q82, Q83, Q84, Q85, Q86, Q87, Q88, Q89, Q90, Q91, Q92, Q93, Q94, Q95, Q96, Q97, Q98, Q99]), "scope" : qUnion([Q100])});
        }
        {
            var Q0;
            Q0=sQuery(id+"F0.wireOp",VERTEX,"E2.24.14.0");
            var Q1;
            Q1=sQuery(id+"F0.wireOp",VERTEX,"E2.22.16.0");
            var Q2;
            Q2=sQuery(id+"F0.wireOp",VERTEX,"E2.23.7.0");
            var Q3;
            Q3=sQuery(id+"F0.wireOp",VERTEX,"E2.20.2.0");
            var Q4;
            Q4=sQuery(id+"F0.wireOp",VERTEX,"E2.21.9.0");
            var Q5;
            Q5=sQuery(id+"F0.wireOp",VERTEX,"E2.22.0.0");
            var Q6;
            Q6=sQuery(id+"F0.wireOp",VERTEX,"E2.21.10.0");
            var Q7;
            Q7=sQuery(id+"F0.wireOp",VERTEX,"E2.20.19.0");
            var Q8;
            Q8=sQuery(id+"F0.wireOp",VERTEX,"E2.20.3.0");
            var Q9;
            Q9=sQuery(id+"F0.wireOp",VERTEX,"E2.23.8.0");
            var Q10;
            Q10=sQuery(id+"F0.wireOp",VERTEX,"E2.22.17.0");
            var Q11;
            Q11=sQuery(id+"F0.wireOp",VERTEX,"E2.22.1.0");
            var Q12;
            Q12=sQuery(id+"F0.wireOp",VERTEX,"E2.24.15.0");
            var Q13;
            Q13=sQuery(id+"F0.wireOp",VERTEX,"E2.21.11.0");
            var Q14;
            Q14=sQuery(id+"F0.wireOp",VERTEX,"E2.20.4.0");
            var Q15;
            Q15=sQuery(id+"F0.wireOp",VERTEX,"E2.24.0.0");
            var Q16;
            Q16=sQuery(id+"F0.wireOp",VERTEX,"E2.23.9.0");
            var Q17;
            Q17=sQuery(id+"F0.wireOp",VERTEX,"E2.22.18.0");
            var Q18;
            Q18=sQuery(id+"F0.wireOp",VERTEX,"E2.22.2.0");
            var Q19;
            Q19=sQuery(id+"F0.wireOp",VERTEX,"E2.24.16.0");
            var Q20;
            Q20=sQuery(id+"F0.wireOp",VERTEX,"E2.21.12.0");
            var Q21;
            Q21=sQuery(id+"F0.wireOp",VERTEX,"E2.20.5.0");
            var Q22;
            Q22=sQuery(id+"F0.wireOp",VERTEX,"E2.24.1.0");
            var Q23;
            Q23=sQuery(id+"F0.wireOp",VERTEX,"E2.23.10.0");
            var Q24;
            Q24=sQuery(id+"F0.wireOp",VERTEX,"E2.22.19.0");
            var Q25;
            Q25=sQuery(id+"F0.wireOp",VERTEX,"E2.22.3.0");
            var Q26;
            Q26=sQuery(id+"F0.wireOp",VERTEX,"E2.24.17.0");
            var Q27;
            Q27=sQuery(id+"F0.wireOp",VERTEX,"E2.21.13.0");
            var Q28;
            Q28=sQuery(id+"F0.wireOp",VERTEX,"E2.20.6.0");
            var Q29;
            Q29=sQuery(id+"F0.wireOp",VERTEX,"E2.24.2.0");
            var Q30;
            Q30=sQuery(id+"F0.wireOp",VERTEX,"E2.23.11.0");
            var Q31;
            Q31=sQuery(id+"F0.wireOp",VERTEX,"E2.22.4.0");
            var Q32;
            Q32=sQuery(id+"F0.wireOp",VERTEX,"E2.24.18.0");
            var Q33;
            Q33=sQuery(id+"F0.wireOp",VERTEX,"E2.20.7.0");
            var Q34;
            Q34=sQuery(id+"F0.wireOp",VERTEX,"E2.22.5.0");
            var Q35;
            Q35=sQuery(id+"F0.wireOp",VERTEX,"E2.21.14.0");
            var Q36;
            Q36=sQuery(id+"F0.wireOp",VERTEX,"E2.24.19.0");
            var Q37;
            Q37=sQuery(id+"F0.wireOp",VERTEX,"E2.24.3.0");
            var Q38;
            Q38=sQuery(id+"F0.wireOp",VERTEX,"E2.23.12.0");
            var Q39;
            Q39=sQuery(id+"F0.wireOp",VERTEX,"E2.20.8.0");
            var Q40;
            Q40=sQuery(id+"F0.wireOp",VERTEX,"E2.22.6.0");
            var Q41;
            Q41=sQuery(id+"F0.wireOp",VERTEX,"E2.21.15.0");
            var Q42;
            Q42=sQuery(id+"F0.wireOp",VERTEX,"E2.24.4.0");
            var Q43;
            Q43=sQuery(id+"F0.wireOp",VERTEX,"E2.23.13.0");
            var Q44;
            Q44=sQuery(id+"F0.wireOp",VERTEX,"E2.20.9.0");
            var Q45;
            Q45=sQuery(id+"F0.wireOp",VERTEX,"E2.21.16.0");
            var Q46;
            Q46=sQuery(id+"F0.wireOp",VERTEX,"E2.22.7.0");
            var Q47;
            Q47=sQuery(id+"F0.wireOp",VERTEX,"E2.21.0.0");
            var Q48;
            Q48=sQuery(id+"F0.wireOp",VERTEX,"E2.24.5.0");
            var Q49;
            Q49=sQuery(id+"F0.wireOp",VERTEX,"E2.23.14.0");
            var Q50;
            Q50=sQuery(id+"F0.wireOp",VERTEX,"E2.20.18.0");
            var Q51;
            Q51=sQuery(id+"F0.wireOp",VERTEX,"E2.20.10.0");
            var Q52;
            Q52=sQuery(id+"F0.wireOp",VERTEX,"E2.22.8.0");
            var Q53;
            Q53=sQuery(id+"F0.wireOp",VERTEX,"E2.21.17.0");
            var Q54;
            Q54=sQuery(id+"F0.wireOp",VERTEX,"E2.21.1.0");
            var Q55;
            Q55=sQuery(id+"F0.wireOp",VERTEX,"E2.24.6.0");
            var Q56;
            Q56=sQuery(id+"F0.wireOp",VERTEX,"E2.23.15.0");
            var Q57;
            Q57=sQuery(id+"F0.wireOp",VERTEX,"E2.20.11.0");
            var Q58;
            Q58=sQuery(id+"F0.wireOp",VERTEX,"E2.23.0.0");
            var Q59;
            Q59=sQuery(id+"F0.wireOp",VERTEX,"E2.22.9.0");
            var Q60;
            Q60=sQuery(id+"F0.wireOp",VERTEX,"E2.21.2.0");
            var Q61;
            Q61=sQuery(id+"F0.wireOp",VERTEX,"E2.21.18.0");
            var Q62;
            Q62=sQuery(id+"F0.wireOp",VERTEX,"E2.24.7.0");
            var Q63;
            Q63=sQuery(id+"F0.wireOp",VERTEX,"E2.23.16.0");
            var Q64;
            Q64=sQuery(id+"F0.wireOp",VERTEX,"E2.21.4.0");
            var Q65;
            Q65=sQuery(id+"F0.wireOp",VERTEX,"E2.20.13.0");
            var Q66;
            Q66=sQuery(id+"F0.wireOp",VERTEX,"E2.23.18.0");
            var Q67;
            Q67=sQuery(id+"F0.wireOp",VERTEX,"E2.23.2.0");
            var Q68;
            Q68=sQuery(id+"F0.wireOp",VERTEX,"E2.22.11.0");
            var Q69;
            Q69=sQuery(id+"F0.wireOp",VERTEX,"E2.24.9.0");
            var Q70;
            Q70=sQuery(id+"F0.wireOp",VERTEX,"E2.20.12.0");
            var Q71;
            Q71=sQuery(id+"F0.wireOp",VERTEX,"E2.23.1.0");
            var Q72;
            Q72=sQuery(id+"F0.wireOp",VERTEX,"E2.22.10.0");
            var Q73;
            Q73=sQuery(id+"F0.wireOp",VERTEX,"E2.21.3.0");
            var Q74;
            Q74=sQuery(id+"F0.wireOp",VERTEX,"E2.21.19.0");
            var Q75;
            Q75=sQuery(id+"F0.wireOp",VERTEX,"E2.24.8.0");
            var Q76;
            Q76=sQuery(id+"F0.wireOp",VERTEX,"E2.23.17.0");
            var Q77;
            Q77=sQuery(id+"F0.wireOp",VERTEX,"E2.21.5.0");
            var Q78;
            Q78=sQuery(id+"F0.wireOp",VERTEX,"E2.20.14.0");
            var Q79;
            Q79=sQuery(id+"F0.wireOp",VERTEX,"E2.23.19.0");
            var Q80;
            Q80=sQuery(id+"F0.wireOp",VERTEX,"E2.23.3.0");
            var Q81;
            Q81=sQuery(id+"F0.wireOp",VERTEX,"E2.22.12.0");
            var Q82;
            Q82=sQuery(id+"F0.wireOp",VERTEX,"E2.24.10.0");
            var Q83;
            Q83=sQuery(id+"F0.wireOp",VERTEX,"E2.21.6.0");
            var Q84;
            Q84=sQuery(id+"F0.wireOp",VERTEX,"E2.20.15.0");
            var Q85;
            Q85=sQuery(id+"F0.wireOp",VERTEX,"E2.23.4.0");
            var Q86;
            Q86=sQuery(id+"F0.wireOp",VERTEX,"E2.22.13.0");
            var Q87;
            Q87=sQuery(id+"F0.wireOp",VERTEX,"E2.24.11.0");
            var Q88;
            Q88=sQuery(id+"F0.wireOp",VERTEX,"E2.21.7.0");
            var Q89;
            Q89=sQuery(id+"F0.wireOp",VERTEX,"E2.20.16.0");
            var Q90;
            Q90=sQuery(id+"F0.wireOp",VERTEX,"E2.20.0.0");
            var Q91;
            Q91=sQuery(id+"F0.wireOp",VERTEX,"E2.23.5.0");
            var Q92;
            Q92=sQuery(id+"F0.wireOp",VERTEX,"E2.22.14.0");
            var Q93;
            Q93=sQuery(id+"F0.wireOp",VERTEX,"E2.24.12.0");
            var Q94;
            Q94=sQuery(id+"F0.wireOp",VERTEX,"E2.23.6.0");
            var Q95;
            Q95=sQuery(id+"F0.wireOp",VERTEX,"E2.22.15.0");
            var Q96;
            Q96=sQuery(id+"F0.wireOp",VERTEX,"E2.24.13.0");
            var Q97;
            Q97=sQuery(id+"F0.wireOp",VERTEX,"E2.21.8.0");
            var Q98;
            Q98=sQuery(id+"F0.wireOp",VERTEX,"E2.20.17.0");
            var Q99;
            Q99=sQuery(id+"F0.wireOp",VERTEX,"E2.20.1.0");
            var Q100;
            Q100=makeQuery(id+"F1.opExtrude","SWEPT_BODY",BODY,{"disambiguationData":[OSD([sQuery(id+"F0.wireOp",EDGE,"E0.bottom"),sQuery(id+"F0.wireOp",EDGE,"E0.top"),sQuery(id+"F0.wireOp",EDGE,"E0.left"),sQuery(id+"F0.wireOp",EDGE,"E0.right")])]});
            hole(context, id + "F6", {"style" : HoleStyle.SIMPLE, "endStyle" : HoleEndStyle.THROUGH, "oppositeDirection" : true, "standardTappedOrClearance" : lookupTablePath({ "standard" : "ANSI", "fit" : "Close", "size" : "1/4", "type" : "Clearance" }), "standardBlindInLast" : lookupTablePath({ "fit" : "Close", "standard" : "ANSI", "size" : "1/4", "type" : "Clearance" }), "holeDiameter" : 6.53 * mm, "isTappedThrough" : true, "tappedDepth" : 12.7 * mm, "tapClearance" : 3, "startFromSketch" : true, "locations" : qUnion([Q0, Q1, Q2, Q3, Q4, Q5, Q6, Q7, Q8, Q9, Q10, Q11, Q12, Q13, Q14, Q15, Q16, Q17, Q18, Q19, Q20, Q21, Q22, Q23, Q24, Q25, Q26, Q27, Q28, Q29, Q30, Q31, Q32, Q33, Q34, Q35, Q36, Q37, Q38, Q39, Q40, Q41, Q42, Q43, Q44, Q45, Q46, Q47, Q48, Q49, Q50, Q51, Q52, Q53, Q54, Q55, Q56, Q57, Q58, Q59, Q60, Q61, Q62, Q63, Q64, Q65, Q66, Q67, Q68, Q69, Q70, Q71, Q72, Q73, Q74, Q75, Q76, Q77, Q78, Q79, Q80, Q81, Q82, Q83, Q84, Q85, Q86, Q87, Q88, Q89, Q90, Q91, Q92, Q93, Q94, Q95, Q96, Q97, Q98, Q99]), "scope" : qUnion([Q100])});
        }
        {
            var Q0;
            Q0=sQuery(id+"F0.wireOp",VERTEX,"E2.9.21.0");
            var Q1;
            Q1=sQuery(id+"F0.wireOp",VERTEX,"E2.7.23.0");
            var Q2;
            Q2=sQuery(id+"F0.wireOp",VERTEX,"E2.0.23.0");
            var Q3;
            Q3=sQuery(id+"F0.wireOp",VERTEX,"E2.2.21.0");
            var Q4;
            Q4=sQuery(id+"F0.wireOp",VERTEX,"E2.9.22.0");
            var Q5;
            Q5=sQuery(id+"F0.wireOp",VERTEX,"E2.7.24.0");
            var Q6;
            Q6=sQuery(id+"F0.wireOp",VERTEX,"E2.11.20.0");
            var Q7;
            Q7=sQuery(id+"F0.wireOp",VERTEX,"E2.0.24.0");
            var Q8;
            Q8=sQuery(id+"F0.wireOp",VERTEX,"E2.4.20.0");
            var Q9;
            Q9=sQuery(id+"F0.wireOp",VERTEX,"E2.2.22.0");
            var Q10;
            Q10=sQuery(id+"F0.wireOp",VERTEX,"E2.9.23.0");
            var Q11;
            Q11=sQuery(id+"F0.wireOp",VERTEX,"E2.11.21.0");
            var Q12;
            Q12=sQuery(id+"F0.wireOp",VERTEX,"E2.4.21.0");
            var Q13;
            Q13=sQuery(id+"F0.wireOp",VERTEX,"E2.2.23.0");
            var Q14;
            Q14=sQuery(id+"F0.wireOp",VERTEX,"E2.9.24.0");
            var Q15;
            Q15=sQuery(id+"F0.wireOp",VERTEX,"E2.11.22.0");
            var Q16;
            Q16=sQuery(id+"F0.wireOp",VERTEX,"E2.13.20.0");
            var Q17;
            Q17=sQuery(id+"F0.wireOp",VERTEX,"E2.4.22.0");
            var Q18;
            Q18=sQuery(id+"F0.wireOp",VERTEX,"E2.2.24.0");
            var Q19;
            Q19=sQuery(id+"F0.wireOp",VERTEX,"E2.6.20.0");
            var Q20;
            Q20=sQuery(id+"F0.wireOp",VERTEX,"E2.11.23.0");
            var Q21;
            Q21=sQuery(id+"F0.wireOp",VERTEX,"E2.13.21.0");
            var Q22;
            Q22=sQuery(id+"F0.wireOp",VERTEX,"E2.4.23.0");
            var Q23;
            Q23=sQuery(id+"F0.wireOp",VERTEX,"E2.6.21.0");
            var Q24;
            Q24=sQuery(id+"F0.wireOp",VERTEX,"E2.13.22.0");
            var Q25;
            Q25=sQuery(id+"F0.wireOp",VERTEX,"E2.11.24.0");
            var Q26;
            Q26=sQuery(id+"F0.wireOp",VERTEX,"E2.8.20.0");
            var Q27;
            Q27=sQuery(id+"F0.wireOp",VERTEX,"E2.6.22.0");
            var Q28;
            Q28=sQuery(id+"F0.wireOp",VERTEX,"E2.13.23.0");
            var Q29;
            Q29=sQuery(id+"F0.wireOp",VERTEX,"E2.4.24.0");
            var Q30;
            Q30=sQuery(id+"F0.wireOp",VERTEX,"E2.13.24.0");
            var Q31;
            Q31=sQuery(id+"F0.wireOp",VERTEX,"E2.1.20.0");
            var Q32;
            Q32=sQuery(id+"F0.wireOp",VERTEX,"E2.8.21.0");
            var Q33;
            Q33=sQuery(id+"F0.wireOp",VERTEX,"E2.6.23.0");
            var Q34;
            Q34=sQuery(id+"F0.wireOp",VERTEX,"E2.1.21.0");
            var Q35;
            Q35=sQuery(id+"F0.wireOp",VERTEX,"E2.8.22.0");
            var Q36;
            Q36=sQuery(id+"F0.wireOp",VERTEX,"E2.6.24.0");
            var Q37;
            Q37=sQuery(id+"F0.wireOp",VERTEX,"E2.10.20.0");
            var Q38;
            Q38=sQuery(id+"F0.wireOp",VERTEX,"E2.1.24.0");
            var Q39;
            Q39=sQuery(id+"F0.wireOp",VERTEX,"E2.3.22.0");
            var Q40;
            Q40=sQuery(id+"F0.wireOp",VERTEX,"E2.5.20.0");
            var Q41;
            Q41=sQuery(id+"F0.wireOp",VERTEX,"E2.10.23.0");
            var Q42;
            Q42=sQuery(id+"F0.wireOp",VERTEX,"E2.12.21.0");
            var Q43;
            Q43=sQuery(id+"F0.wireOp",VERTEX,"E2.3.20.0");
            var Q44;
            Q44=sQuery(id+"F0.wireOp",VERTEX,"E2.1.22.0");
            var Q45;
            Q45=sQuery(id+"F0.wireOp",VERTEX,"E2.8.23.0");
            var Q46;
            Q46=sQuery(id+"F0.wireOp",VERTEX,"E2.10.21.0");
            var Q47;
            Q47=sQuery(id+"F0.wireOp",VERTEX,"E2.3.23.0");
            var Q48;
            Q48=sQuery(id+"F0.wireOp",VERTEX,"E2.5.21.0");
            var Q49;
            Q49=sQuery(id+"F0.wireOp",VERTEX,"E2.10.24.0");
            var Q50;
            Q50=sQuery(id+"F0.wireOp",VERTEX,"E2.12.22.0");
            var Q51;
            Q51=sQuery(id+"F0.wireOp",VERTEX,"E2.3.21.0");
            var Q52;
            Q52=sQuery(id+"F0.wireOp",VERTEX,"E2.1.23.0");
            var Q53;
            Q53=sQuery(id+"F0.wireOp",VERTEX,"E2.8.24.0");
            var Q54;
            Q54=sQuery(id+"F0.wireOp",VERTEX,"E2.10.22.0");
            var Q55;
            Q55=sQuery(id+"F0.wireOp",VERTEX,"E2.12.20.0");
            var Q56;
            Q56=sQuery(id+"F0.wireOp",VERTEX,"E2.3.24.0");
            var Q57;
            Q57=sQuery(id+"F0.wireOp",VERTEX,"E2.5.22.0");
            var Q58;
            Q58=sQuery(id+"F0.wireOp",VERTEX,"E2.7.20.0");
            var Q59;
            Q59=sQuery(id+"F0.wireOp",VERTEX,"E2.12.23.0");
            var Q60;
            Q60=sQuery(id+"F0.wireOp",VERTEX,"E2.0.20.0");
            var Q61;
            Q61=sQuery(id+"F0.wireOp",VERTEX,"E2.5.23.0");
            var Q62;
            Q62=sQuery(id+"F0.wireOp",VERTEX,"E2.7.21.0");
            var Q63;
            Q63=sQuery(id+"F0.wireOp",VERTEX,"E2.12.24.0");
            var Q64;
            Q64=sQuery(id+"F0.wireOp",VERTEX,"E2.0.21.0");
            var Q65;
            Q65=sQuery(id+"F0.wireOp",VERTEX,"E2.5.24.0");
            var Q66;
            Q66=sQuery(id+"F0.wireOp",VERTEX,"E2.9.20.0");
            var Q67;
            Q67=sQuery(id+"F0.wireOp",VERTEX,"E2.7.22.0");
            var Q68;
            Q68=sQuery(id+"F0.wireOp",VERTEX,"E2.0.22.0");
            var Q69;
            Q69=sQuery(id+"F0.wireOp",VERTEX,"E2.2.20.0");
            var Q70;
            Q70=makeQuery(id+"F1.opExtrude","SWEPT_BODY",BODY,{"disambiguationData":[OSD([sQuery(id+"F0.wireOp",EDGE,"E0.bottom"),sQuery(id+"F0.wireOp",EDGE,"E0.top"),sQuery(id+"F0.wireOp",EDGE,"E0.left"),sQuery(id+"F0.wireOp",EDGE,"E0.right")])]});
            hole(context, id + "F7", {"style" : HoleStyle.SIMPLE, "endStyle" : HoleEndStyle.THROUGH, "oppositeDirection" : true, "standardTappedOrClearance" : lookupTablePath({ "standard" : "ANSI", "fit" : "Close", "size" : "1/4", "type" : "Clearance" }), "standardBlindInLast" : lookupTablePath({ "fit" : "Close", "standard" : "ANSI", "size" : "1/4", "type" : "Clearance" }), "holeDiameter" : 6.53 * mm, "isTappedThrough" : true, "tappedDepth" : 12.7 * mm, "tapClearance" : 3, "startFromSketch" : true, "locations" : qUnion([Q0, Q1, Q2, Q3, Q4, Q5, Q6, Q7, Q8, Q9, Q10, Q11, Q12, Q13, Q14, Q15, Q16, Q17, Q18, Q19, Q20, Q21, Q22, Q23, Q24, Q25, Q26, Q27, Q28, Q29, Q30, Q31, Q32, Q33, Q34, Q35, Q36, Q37, Q38, Q39, Q40, Q41, Q42, Q43, Q44, Q45, Q46, Q47, Q48, Q49, Q50, Q51, Q52, Q53, Q54, Q55, Q56, Q57, Q58, Q59, Q60, Q61, Q62, Q63, Q64, Q65, Q66, Q67, Q68, Q69]), "scope" : qUnion([Q70])});
        }
        {
            var Q0;
            Q0=sQuery(id+"F0.wireOp",VERTEX,"E2.14.24.0");
            var Q1;
            Q1=sQuery(id+"F0.wireOp",VERTEX,"E2.16.22.0");
            var Q2;
            Q2=sQuery(id+"F0.wireOp",VERTEX,"E2.18.20.0");
            var Q3;
            Q3=sQuery(id+"F0.wireOp",VERTEX,"E2.18.21.0");
            var Q4;
            Q4=sQuery(id+"F0.wireOp",VERTEX,"E2.16.23.0");
            var Q5;
            Q5=sQuery(id+"F0.wireOp",VERTEX,"E2.23.24.0");
            var Q6;
            Q6=sQuery(id+"F0.wireOp",VERTEX,"E2.18.22.0");
            var Q7;
            Q7=sQuery(id+"F0.wireOp",VERTEX,"E2.16.24.0");
            var Q8;
            Q8=sQuery(id+"F0.wireOp",VERTEX,"E2.20.20.0");
            var Q9;
            Q9=sQuery(id+"F0.wireOp",VERTEX,"E2.18.23.0");
            var Q10;
            Q10=sQuery(id+"F0.wireOp",VERTEX,"E2.20.21.0");
            var Q11;
            Q11=sQuery(id+"F0.wireOp",VERTEX,"E2.18.24.0");
            var Q12;
            Q12=sQuery(id+"F0.wireOp",VERTEX,"E2.20.22.0");
            var Q13;
            Q13=sQuery(id+"F0.wireOp",VERTEX,"E2.22.20.0");
            var Q14;
            Q14=sQuery(id+"F0.wireOp",VERTEX,"E2.15.20.0");
            var Q15;
            Q15=sQuery(id+"F0.wireOp",VERTEX,"E2.22.21.0");
            var Q16;
            Q16=sQuery(id+"F0.wireOp",VERTEX,"E2.20.23.0");
            var Q17;
            Q17=sQuery(id+"F0.wireOp",VERTEX,"E2.15.21.0");
            var Q18;
            Q18=sQuery(id+"F0.wireOp",VERTEX,"E2.22.22.0");
            var Q19;
            Q19=sQuery(id+"F0.wireOp",VERTEX,"E2.20.24.0");
            var Q20;
            Q20=sQuery(id+"F0.wireOp",VERTEX,"E2.24.20.0");
            var Q21;
            Q21=sQuery(id+"F0.wireOp",VERTEX,"E2.15.22.0");
            var Q22;
            Q22=sQuery(id+"F0.wireOp",VERTEX,"E2.17.20.0");
            var Q23;
            Q23=sQuery(id+"F0.wireOp",VERTEX,"E2.22.23.0");
            var Q24;
            Q24=sQuery(id+"F0.wireOp",VERTEX,"E2.24.21.0");
            var Q25;
            Q25=sQuery(id+"F0.wireOp",VERTEX,"E2.23.23.0");
            var Q26;
            Q26=sQuery(id+"F0.wireOp",VERTEX,"E2.15.23.0");
            var Q27;
            Q27=sQuery(id+"F0.wireOp",VERTEX,"E2.17.21.0");
            var Q28;
            Q28=sQuery(id+"F0.wireOp",VERTEX,"E2.22.24.0");
            var Q29;
            Q29=sQuery(id+"F0.wireOp",VERTEX,"E2.24.22.0");
            var Q30;
            Q30=sQuery(id+"F0.wireOp",VERTEX,"E2.15.24.0");
            var Q31;
            Q31=sQuery(id+"F0.wireOp",VERTEX,"E2.17.22.0");
            var Q32;
            Q32=sQuery(id+"F0.wireOp",VERTEX,"E2.19.20.0");
            var Q33;
            Q33=sQuery(id+"F0.wireOp",VERTEX,"E2.24.23.0");
            var Q34;
            Q34=sQuery(id+"F0.wireOp",VERTEX,"E2.17.24.0");
            var Q35;
            Q35=sQuery(id+"F0.wireOp",VERTEX,"E2.19.22.0");
            var Q36;
            Q36=sQuery(id+"F0.wireOp",VERTEX,"E2.21.20.0");
            var Q37;
            Q37=sQuery(id+"F0.wireOp",VERTEX,"E2.14.20.0");
            var Q38;
            Q38=sQuery(id+"F0.wireOp",VERTEX,"E2.17.23.0");
            var Q39;
            Q39=sQuery(id+"F0.wireOp",VERTEX,"E2.19.21.0");
            var Q40;
            Q40=sQuery(id+"F0.wireOp",VERTEX,"E2.24.24.0");
            var Q41;
            Q41=sQuery(id+"F0.wireOp",VERTEX,"E2.19.23.0");
            var Q42;
            Q42=sQuery(id+"F0.wireOp",VERTEX,"E2.21.21.0");
            var Q43;
            Q43=sQuery(id+"F0.wireOp",VERTEX,"E2.14.21.0");
            var Q44;
            Q44=sQuery(id+"F0.wireOp",VERTEX,"E2.19.24.0");
            var Q45;
            Q45=sQuery(id+"F0.wireOp",VERTEX,"E2.23.20.0");
            var Q46;
            Q46=sQuery(id+"F0.wireOp",VERTEX,"E2.21.22.0");
            var Q47;
            Q47=sQuery(id+"F0.wireOp",VERTEX,"E2.23.21.0");
            var Q48;
            Q48=sQuery(id+"F0.wireOp",VERTEX,"E2.21.23.0");
            var Q49;
            Q49=sQuery(id+"F0.wireOp",VERTEX,"E2.14.22.0");
            var Q50;
            Q50=sQuery(id+"F0.wireOp",VERTEX,"E2.16.20.0");
            var Q51;
            Q51=sQuery(id+"F0.wireOp",VERTEX,"E2.23.22.0");
            var Q52;
            Q52=sQuery(id+"F0.wireOp",VERTEX,"E2.21.24.0");
            var Q53;
            Q53=sQuery(id+"F0.wireOp",VERTEX,"E2.14.23.0");
            var Q54;
            Q54=sQuery(id+"F0.wireOp",VERTEX,"E2.16.21.0");
            var Q55;
            Q55=makeQuery(id+"F1.opExtrude","SWEPT_BODY",BODY,{"disambiguationData":[OSD([sQuery(id+"F0.wireOp",EDGE,"E0.bottom"),sQuery(id+"F0.wireOp",EDGE,"E0.top"),sQuery(id+"F0.wireOp",EDGE,"E0.left"),sQuery(id+"F0.wireOp",EDGE,"E0.right")])]});
            hole(context, id + "F8", {"style" : HoleStyle.SIMPLE, "endStyle" : HoleEndStyle.THROUGH, "oppositeDirection" : true, "standardTappedOrClearance" : lookupTablePath({ "standard" : "ANSI", "fit" : "Close", "size" : "1/4", "type" : "Clearance" }), "standardBlindInLast" : lookupTablePath({ "fit" : "Close", "standard" : "ANSI", "size" : "1/4", "type" : "Clearance" }), "holeDiameter" : 6.53 * mm, "isTappedThrough" : true, "tappedDepth" : 12.7 * mm, "tapClearance" : 3, "startFromSketch" : true, "locations" : qUnion([Q0, Q1, Q2, Q3, Q4, Q5, Q6, Q7, Q8, Q9, Q10, Q11, Q12, Q13, Q14, Q15, Q16, Q17, Q18, Q19, Q20, Q21, Q22, Q23, Q24, Q25, Q26, Q27, Q28, Q29, Q30, Q31, Q32, Q33, Q34, Q35, Q36, Q37, Q38, Q39, Q40, Q41, Q42, Q43, Q44, Q45, Q46, Q47, Q48, Q49, Q50, Q51, Q52, Q53, Q54]), "scope" : qUnion([Q55])});
        }
    });
